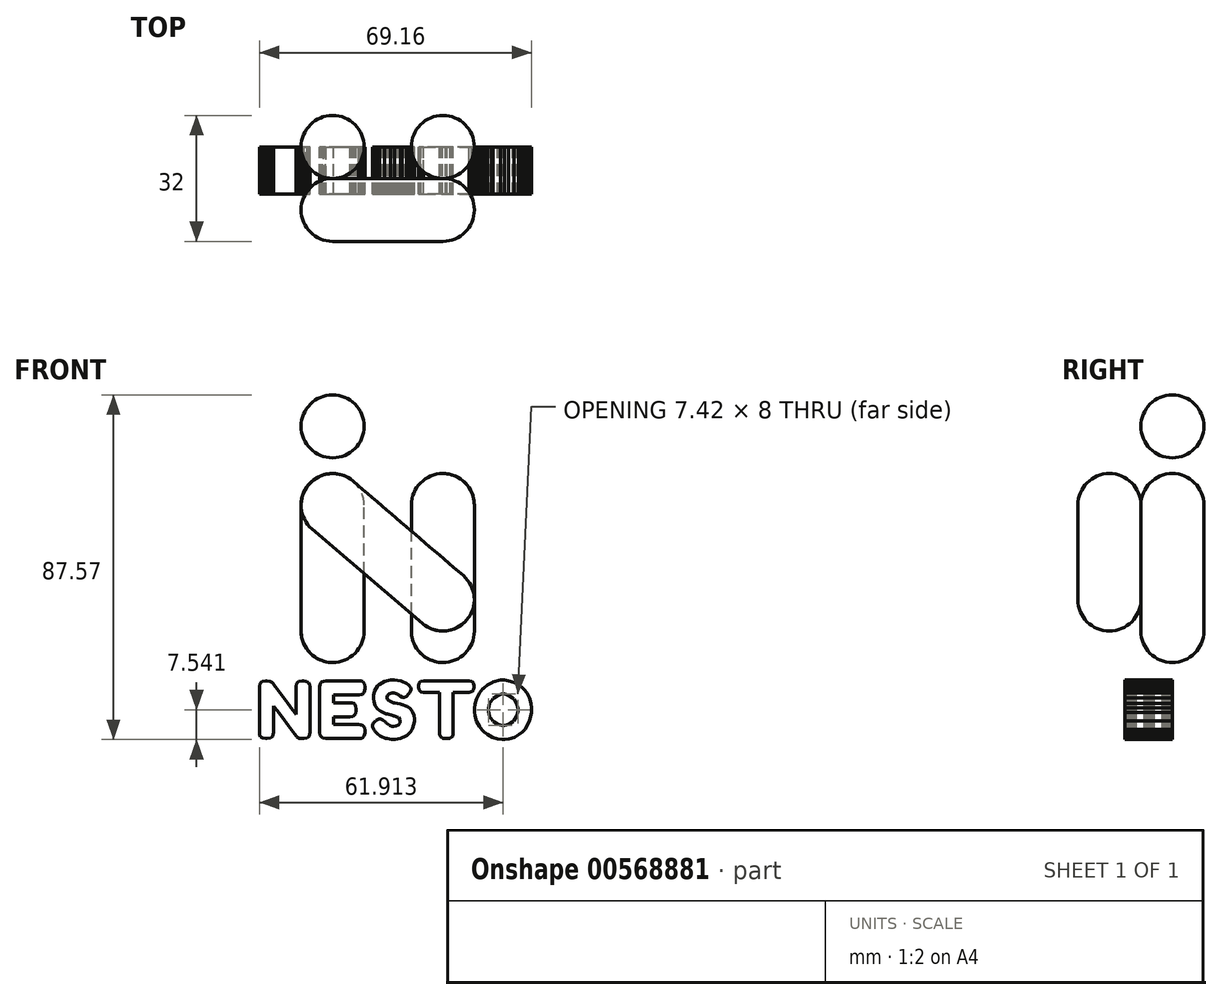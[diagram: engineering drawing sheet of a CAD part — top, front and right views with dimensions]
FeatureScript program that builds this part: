
annotation { "Feature Type Name" : "Feature", "Feature Type Description" : "" }
export const myFeature = defineFeature(function(context is Context, id is Id, definition is map)
    precondition{}
    {
        {
            var Q0;
            Q0=qCreatedBy(makeId("Front.planeOp"),FACE);
            var sketch = newSketch(context, id + "F0", { "sketchPlane" : qUnion([Q0])});
            skLineSegment(sketch, "E0.bottom", {"start": v(0, 0) * mm, "end": v(16, 0) * mm, "construction": true});
            skLineSegment(sketch, "E0.top", {"start": v(0, 32) * mm, "end": v(16, 32) * mm, "construction": true});
            skLineSegment(sketch, "E0.left", {"start": v(0, 0) * mm, "end": v(0, 32) * mm});
            skLineSegment(sketch, "E0.right", {"start": v(16, 0) * mm, "end": v(16, 32) * mm});
            skArc(sketch, "E1", {"start": v(0, 32) * mm, "mid": v(8, 40) * mm, "end": v(16, 32) * mm});
            skArc(sketch, "E2", {"start": v(0, 0) * mm, "mid": v(8, -8) * mm, "end": v(16, 0) * mm});
            skArc(sketch, "E3.1.0.0", {"start": v(28, 0) * mm, "mid": v(36, -8) * mm, "end": v(44, 0) * mm});
            skArc(sketch, "E3.1.0.1", {"start": v(28, 32) * mm, "mid": v(36, 40) * mm, "end": v(44, 32) * mm});
            skLineSegment(sketch, "E3.1.0.2", {"start": v(44, 0) * mm, "end": v(44, 32) * mm});
            skLineSegment(sketch, "E3.1.0.3", {"start": v(28, 0) * mm, "end": v(28, 32) * mm});
            skLineSegment(sketch, "E3.1.0.4", {"start": v(28, 32) * mm, "end": v(44, 32) * mm, "construction": true});
            skLineSegment(sketch, "E3.1.0.5", {"start": v(28, 0) * mm, "end": v(44, 0) * mm, "construction": true});
            skLineSegment(sketch, "E3.direction1", {"start": v(0, 0) * mm, "end": v(28, 0) * mm, "construction": true});
            skLineSegment(sketch, "E4", {"start": v(8, 40) * mm, "end": v(8, -8) * mm});
            skLineSegment(sketch, "E5", {"start": v(36, 40) * mm, "end": v(36, -8) * mm});
            skLineSegment(sketch, "E6", {"start": v(8, 32) * mm, "end": v(36, 8) * mm, "construction": true});
            skCircle(sketch, "E7", {"center": v(36, 8) * mm, "radius": 8 * mm, "construction": true});
            skCircle(sketch, "E8", {"center": v(8, 52) * mm, "radius": 8 * mm});
            skLineSegment(sketch, "E9", {"start": v(8, 60) * mm, "end": v(8, 44) * mm});
            skSolve(sketch);
        }
        {
            var Q0;
            {var subQ0=sQuery(id+"F0.wireOp",EDGE,"E0.left");Q0=makeQuery(id+"F0.imprint","IMPRINT",FACE,{"disambiguationData":[TD([[makeQuery(id+"F0.imprint","IMPRINT",EDGE,{"derivedFrom":subQ0}),-1.0]])]});}
            var Q1;
            Q1=sQuery(id+"F0.wireOp",EDGE,"E4");
            revolve(context, id + "F1", {"entities" : qUnion([Q0]), "axis" : qUnion([Q1]), "revolveType" : RevolveType.FULL});
        }
        {
            var Q0;
            {var subQ0=sQuery(id+"F0.wireOp",EDGE,"E3.1.0.3");Q0=makeQuery(id+"F0.imprint","IMPRINT",FACE,{"disambiguationData":[TD([[makeQuery(id+"F0.imprint","IMPRINT",EDGE,{"derivedFrom":subQ0}),-1.0]])]});}
            var Q1;
            Q1=sQuery(id+"F0.wireOp",EDGE,"E5");
            revolve(context, id + "F2", {"entities" : qUnion([Q0]), "axis" : qUnion([Q1]), "revolveType" : RevolveType.FULL});
        }
        {
            var Q0;
            {var subQ0=sQuery(id+"F0.wireOp",EDGE,"E9");Q0=makeQuery(id+"F0.imprint","IMPRINT",FACE,{"disambiguationData":[TD([[makeQuery(id+"F0.imprint","IMPRINT",EDGE,{"derivedFrom":subQ0}),-1.0]])]});}
            var Q1;
            Q1=sQuery(id+"F0.wireOp",EDGE,"E9");
            revolve(context, id + "F3", {"entities" : qUnion([Q0]), "axis" : qUnion([Q1]), "revolveType" : RevolveType.FULL});
        }
        {
            var Q0;
            Q0=qCreatedBy(makeId("Front.planeOp"),FACE);
            var sketch = newSketch(context, id + "F4", { "sketchPlane" : qUnion([Q0])});
            skLineSegment(sketch, "E10.0", {"start": v(1.93, 37.2) * mm, "end": v(42.07, 2.8) * mm});
            skArc(sketch, "E11.0", {"start": v(42.07, 2.8) * mm, "mid": v(43.98, 8.61) * mm, "end": v(41.2, 14.07) * mm});
            skArc(sketch, "E12", {"start": v(13.2, 38.07) * mm, "mid": v(7.39, 39.98) * mm, "end": v(1.93, 37.2) * mm});
            skLineSegment(sketch, "E13", {"start": v(8, 32) * mm, "end": v(13.2, 38.07) * mm, "construction": true});
            skLineSegment(sketch, "E14", {"start": v(13.2, 38.07) * mm, "end": v(41.2, 14.07) * mm});
            skSolve(sketch);
        }
        {
            var Q0;
            Q0=makeQuery(id+"F4.imprint","IMPRINT",FACE,{"disambiguationData":[TD([[makeQuery(id+"F4.imprint","IMPRINT",EDGE,{"derivedFrom":sQuery(id+"F4.wireOp",EDGE,"E10.0")}),1.0]])]});
            var Q1;
            Q1=sQuery(id+"F4.wireOp",EDGE,"E10.0");
            revolve(context, id + "F5", {"entities" : qUnion([Q0]), "axis" : qUnion([Q1]), "revolveType" : RevolveType.FULL});
        }
        {
            var Q0;
            Q0=makeQuery(id+"F5.opRevolve","SWEPT_BODY",BODY,{"disambiguationData":[OSD([sQuery(id+"F4.wireOp",EDGE,"E10.0"),sQuery(id+"F4.wireOp",EDGE,"E11.0"),sQuery(id+"F4.wireOp",EDGE,"E12"),sQuery(id+"F4.wireOp",EDGE,"E14")])]});
            transform(context, id + "F6", {"entities" : qUnion([Q0]), "transformType" : TransformType.TRANSLATION_3D, "dx" : 0 * mm, "dy" : -16 * mm, "dz" : 0 * mm, "makeCopy" : false});
        }
        {
            var Q0;
            Q0=qCreatedBy(makeId("Front.planeOp"),FACE);
            var sketch = newSketch(context, id + "F7", { "sketchPlane" : qUnion([Q0])});
            skLineSegment(sketch, "E15", {"start": v(-1.05, 0.28) * mm, "end": v(-1.05, 0.28) * mm});
            skLineSegment(sketch, "E16", {"start": v(-1.05, 0.28) * mm, "end": v(-1.03, 0.3) * mm});
            skLineSegment(sketch, "E17", {"start": v(-1.03, 0.3) * mm, "end": v(-1.02, 0.3) * mm});
            skLineSegment(sketch, "E18", {"start": v(-1.02, 0.3) * mm, "end": v(-1.02, 0.3) * mm});
            skLineSegment(sketch, "E19", {"start": v(-1.02, 0.3) * mm, "end": v(-1, 0.3) * mm});
            skLineSegment(sketch, "E20", {"start": v(-1, 0.3) * mm, "end": v(-0.98, 0.3) * mm});
            skLineSegment(sketch, "E21", {"start": v(-0.98, 0.3) * mm, "end": v(-0.97, 0.3) * mm});
            skLineSegment(sketch, "E22", {"start": v(-0.97, 0.3) * mm, "end": v(-0.95, 0.3) * mm});
            skLineSegment(sketch, "E23", {"start": v(-0.95, 0.3) * mm, "end": v(-0.94, 0.3) * mm});
            skLineSegment(sketch, "E24", {"start": v(-0.94, 0.3) * mm, "end": v(-0.94, 0.3) * mm});
            skLineSegment(sketch, "E25", {"start": v(-0.94, 0.3) * mm, "end": v(-0.92, 0.3) * mm});
            skLineSegment(sketch, "E26", {"start": v(-0.92, 0.3) * mm, "end": v(-0.92, 0.3) * mm});
            skLineSegment(sketch, "E27", {"start": v(-0.92, 0.3) * mm, "end": v(-0.92, 0.29) * mm});
            skLineSegment(sketch, "E28", {"start": v(-0.92, 0.29) * mm, "end": v(-0.91, 0.27) * mm});
            skLineSegment(sketch, "E29", {"start": v(-0.91, 0.27) * mm, "end": v(-0.91, 0.27) * mm});
            skLineSegment(sketch, "E30", {"start": v(-0.91, 0.27) * mm, "end": v(-0.9, 0.24) * mm});
            skLineSegment(sketch, "E31", {"start": v(-0.9, 0.24) * mm, "end": v(-0.9, 0.23) * mm});
            skLineSegment(sketch, "E32", {"start": v(-0.9, 0.23) * mm, "end": v(-0.9, -0.23) * mm});
            skLineSegment(sketch, "E33", {"start": v(-0.9, -0.23) * mm, "end": v(-0.9, -0.24) * mm});
            skLineSegment(sketch, "E34", {"start": v(-0.9, -0.24) * mm, "end": v(-0.9, -0.26) * mm});
            skLineSegment(sketch, "E35", {"start": v(-0.9, -0.26) * mm, "end": v(-0.9, -0.26) * mm});
            skLineSegment(sketch, "E36", {"start": v(-0.9, -0.26) * mm, "end": v(-0.92, -0.28) * mm});
            skLineSegment(sketch, "E37", {"start": v(-0.92, -0.28) * mm, "end": v(-0.92, -0.28) * mm});
            skLineSegment(sketch, "E38", {"start": v(-0.92, -0.28) * mm, "end": v(-0.92, -0.29) * mm});
            skLineSegment(sketch, "E39", {"start": v(-0.92, -0.29) * mm, "end": v(-0.94, -0.3) * mm});
            skLineSegment(sketch, "E40", {"start": v(-0.94, -0.3) * mm, "end": v(-0.97, -0.3) * mm});
            skLineSegment(sketch, "E41", {"start": v(-0.97, -0.3) * mm, "end": v(-0.98, -0.3) * mm});
            skLineSegment(sketch, "E42", {"start": v(-0.98, -0.3) * mm, "end": v(-1, -0.3) * mm});
            skLineSegment(sketch, "E43", {"start": v(-1, -0.3) * mm, "end": v(-1.02, -0.3) * mm});
            skLineSegment(sketch, "E44", {"start": v(-1.02, -0.3) * mm, "end": v(-1.03, -0.3) * mm});
            skLineSegment(sketch, "E45", {"start": v(-1.03, -0.3) * mm, "end": v(-1.03, -0.3) * mm});
            skLineSegment(sketch, "E46", {"start": v(-1.03, -0.3) * mm, "end": v(-1.05, -0.29) * mm});
            skLineSegment(sketch, "E47", {"start": v(-1.05, -0.29) * mm, "end": v(-1.05, -0.28) * mm});
            skLineSegment(sketch, "E48", {"start": v(-1.05, -0.28) * mm, "end": v(-1.07, -0.26) * mm});
            skLineSegment(sketch, "E49", {"start": v(-1.07, -0.26) * mm, "end": v(-1.13, -0.17) * mm});
            skLineSegment(sketch, "E50", {"start": v(-1.13, -0.17) * mm, "end": v(-1.2, -0.08) * mm});
            skLineSegment(sketch, "E51", {"start": v(-1.2, -0.08) * mm, "end": v(-1.26, 0) * mm});
            skLineSegment(sketch, "E52", {"start": v(-1.26, 0) * mm, "end": v(-1.28, 0.03) * mm});
            skLineSegment(sketch, "E53", {"start": v(-1.28, 0.03) * mm, "end": v(-1.3, 0.04) * mm});
            skLineSegment(sketch, "E54", {"start": v(-1.3, 0.04) * mm, "end": v(-1.3, -0.23) * mm});
            skLineSegment(sketch, "E55", {"start": v(-1.3, -0.23) * mm, "end": v(-1.3, -0.24) * mm});
            skLineSegment(sketch, "E56", {"start": v(-1.3, -0.24) * mm, "end": v(-1.3, -0.26) * mm});
            skLineSegment(sketch, "E57", {"start": v(-1.3, -0.26) * mm, "end": v(-1.3, -0.26) * mm});
            skLineSegment(sketch, "E58", {"start": v(-1.3, -0.26) * mm, "end": v(-1.3, -0.28) * mm});
            skLineSegment(sketch, "E59", {"start": v(-1.3, -0.28) * mm, "end": v(-1.3, -0.28) * mm});
            skLineSegment(sketch, "E60", {"start": v(-1.3, -0.28) * mm, "end": v(-1.3, -0.29) * mm});
            skLineSegment(sketch, "E61", {"start": v(-1.3, -0.29) * mm, "end": v(-1.33, -0.3) * mm});
            skLineSegment(sketch, "E62", {"start": v(-1.33, -0.3) * mm, "end": v(-1.36, -0.3) * mm});
            skLineSegment(sketch, "E63", {"start": v(-1.36, -0.3) * mm, "end": v(-1.37, -0.3) * mm});
            skLineSegment(sketch, "E64", {"start": v(-1.37, -0.3) * mm, "end": v(-1.38, -0.3) * mm});
            skLineSegment(sketch, "E65", {"start": v(-1.38, -0.3) * mm, "end": v(-1.41, -0.3) * mm});
            skLineSegment(sketch, "E66", {"start": v(-1.41, -0.3) * mm, "end": v(-1.43, -0.29) * mm});
            skLineSegment(sketch, "E67", {"start": v(-1.43, -0.29) * mm, "end": v(-1.43, -0.28) * mm});
            skLineSegment(sketch, "E68", {"start": v(-1.43, -0.28) * mm, "end": v(-1.43, -0.28) * mm});
            skLineSegment(sketch, "E69", {"start": v(-1.43, -0.28) * mm, "end": v(-1.44, -0.26) * mm});
            skLineSegment(sketch, "E70", {"start": v(-1.44, -0.26) * mm, "end": v(-1.44, -0.26) * mm});
            skLineSegment(sketch, "E71", {"start": v(-1.44, -0.26) * mm, "end": v(-1.44, -0.24) * mm});
            skLineSegment(sketch, "E72", {"start": v(-1.44, -0.24) * mm, "end": v(-1.44, -0.23) * mm});
            skLineSegment(sketch, "E73", {"start": v(-1.44, -0.23) * mm, "end": v(-1.44, 0.23) * mm});
            skLineSegment(sketch, "E74", {"start": v(-1.44, 0.23) * mm, "end": v(-1.44, 0.25) * mm});
            skLineSegment(sketch, "E75", {"start": v(-1.44, 0.25) * mm, "end": v(-1.43, 0.28) * mm});
            skLineSegment(sketch, "E76", {"start": v(-1.43, 0.28) * mm, "end": v(-1.43, 0.28) * mm});
            skLineSegment(sketch, "E77", {"start": v(-1.43, 0.28) * mm, "end": v(-1.41, 0.3) * mm});
            skLineSegment(sketch, "E78", {"start": v(-1.41, 0.3) * mm, "end": v(-1.4, 0.3) * mm});
            skLineSegment(sketch, "E79", {"start": v(-1.4, 0.3) * mm, "end": v(-1.4, 0.3) * mm});
            skLineSegment(sketch, "E80", {"start": v(-1.4, 0.3) * mm, "end": v(-1.38, 0.3) * mm});
            skLineSegment(sketch, "E81", {"start": v(-1.38, 0.3) * mm, "end": v(-1.37, 0.3) * mm});
            skLineSegment(sketch, "E82", {"start": v(-1.37, 0.3) * mm, "end": v(-1.36, 0.3) * mm});
            skLineSegment(sketch, "E83", {"start": v(-1.36, 0.3) * mm, "end": v(-1.33, 0.3) * mm});
            skLineSegment(sketch, "E84", {"start": v(-1.33, 0.3) * mm, "end": v(-1.33, 0.3) * mm});
            skLineSegment(sketch, "E85", {"start": v(-1.33, 0.3) * mm, "end": v(-1.3, 0.3) * mm});
            skLineSegment(sketch, "E86", {"start": v(-1.3, 0.3) * mm, "end": v(-1.3, 0.29) * mm});
            skLineSegment(sketch, "E87", {"start": v(-1.3, 0.29) * mm, "end": v(-1.3, 0.29) * mm});
            skLineSegment(sketch, "E88", {"start": v(-1.3, 0.29) * mm, "end": v(-1.3, 0.28) * mm});
            skLineSegment(sketch, "E89", {"start": v(-1.3, 0.28) * mm, "end": v(-1.3, 0.27) * mm});
            skLineSegment(sketch, "E90", {"start": v(-1.3, 0.27) * mm, "end": v(-1.29, 0.27) * mm});
            skLineSegment(sketch, "E91", {"start": v(-1.29, 0.27) * mm, "end": v(-1.27, 0.24) * mm});
            skLineSegment(sketch, "E92", {"start": v(-1.27, 0.24) * mm, "end": v(-1.2, 0.16) * mm});
            skLineSegment(sketch, "E93", {"start": v(-1.2, 0.16) * mm, "end": v(-1.14, 0.07) * mm});
            skLineSegment(sketch, "E94", {"start": v(-1.14, 0.07) * mm, "end": v(-1.1, 0) * mm});
            skLineSegment(sketch, "E95", {"start": v(-1.1, 0) * mm, "end": v(-1.06, -0.04) * mm});
            skLineSegment(sketch, "E96", {"start": v(-1.06, -0.04) * mm, "end": v(-1.05, -0.05) * mm});
            skLineSegment(sketch, "E97", {"start": v(-1.05, -0.05) * mm, "end": v(-1.05, 0.23) * mm});
            skLineSegment(sketch, "E98", {"start": v(-1.05, 0.23) * mm, "end": v(-1.05, 0.25) * mm});
            skLineSegment(sketch, "E99", {"start": v(-1.05, 0.25) * mm, "end": v(-1.05, 0.28) * mm});
            skLineSegment(sketch, "E100", {"start": v(-0.66, -0.16) * mm, "end": v(-0.4, -0.16) * mm});
            skLineSegment(sketch, "E101", {"start": v(-0.4, -0.16) * mm, "end": v(-0.4, -0.16) * mm});
            skLineSegment(sketch, "E102", {"start": v(-0.4, -0.16) * mm, "end": v(-0.37, -0.16) * mm});
            skLineSegment(sketch, "E103", {"start": v(-0.37, -0.16) * mm, "end": v(-0.37, -0.16) * mm});
            skLineSegment(sketch, "E104", {"start": v(-0.37, -0.16) * mm, "end": v(-0.35, -0.17) * mm});
            skLineSegment(sketch, "E105", {"start": v(-0.35, -0.17) * mm, "end": v(-0.35, -0.17) * mm});
            skLineSegment(sketch, "E106", {"start": v(-0.35, -0.17) * mm, "end": v(-0.34, -0.17) * mm});
            skLineSegment(sketch, "E107", {"start": v(-0.34, -0.17) * mm, "end": v(-0.33, -0.19) * mm});
            skLineSegment(sketch, "E108", {"start": v(-0.33, -0.19) * mm, "end": v(-0.33, -0.22) * mm});
            skLineSegment(sketch, "E109", {"start": v(-0.33, -0.22) * mm, "end": v(-0.33, -0.23) * mm});
            skLineSegment(sketch, "E110", {"start": v(-0.33, -0.23) * mm, "end": v(-0.33, -0.24) * mm});
            skLineSegment(sketch, "E111", {"start": v(-0.33, -0.24) * mm, "end": v(-0.33, -0.28) * mm});
            skLineSegment(sketch, "E112", {"start": v(-0.33, -0.28) * mm, "end": v(-0.35, -0.3) * mm});
            skLineSegment(sketch, "E113", {"start": v(-0.35, -0.3) * mm, "end": v(-0.36, -0.3) * mm});
            skLineSegment(sketch, "E114", {"start": v(-0.36, -0.3) * mm, "end": v(-0.36, -0.3) * mm});
            skLineSegment(sketch, "E115", {"start": v(-0.36, -0.3) * mm, "end": v(-0.39, -0.3) * mm});
            skLineSegment(sketch, "E116", {"start": v(-0.39, -0.3) * mm, "end": v(-0.4, -0.3) * mm});
            skLineSegment(sketch, "E117", {"start": v(-0.4, -0.3) * mm, "end": v(-0.73, -0.3) * mm});
            skLineSegment(sketch, "E118", {"start": v(-0.73, -0.3) * mm, "end": v(-0.74, -0.3) * mm});
            skLineSegment(sketch, "E119", {"start": v(-0.74, -0.3) * mm, "end": v(-0.78, -0.3) * mm});
            skLineSegment(sketch, "E120", {"start": v(-0.78, -0.3) * mm, "end": v(-0.8, -0.28) * mm});
            skLineSegment(sketch, "E121", {"start": v(-0.8, -0.28) * mm, "end": v(-0.8, -0.27) * mm});
            skLineSegment(sketch, "E122", {"start": v(-0.8, -0.27) * mm, "end": v(-0.8, -0.27) * mm});
            skLineSegment(sketch, "E123", {"start": v(-0.8, -0.27) * mm, "end": v(-0.8, -0.24) * mm});
            skLineSegment(sketch, "E124", {"start": v(-0.8, -0.24) * mm, "end": v(-0.8, -0.23) * mm});
            skLineSegment(sketch, "E125", {"start": v(-0.8, -0.23) * mm, "end": v(-0.8, 0.23) * mm});
            skLineSegment(sketch, "E126", {"start": v(-0.8, 0.23) * mm, "end": v(-0.8, 0.24) * mm});
            skLineSegment(sketch, "E127", {"start": v(-0.8, 0.24) * mm, "end": v(-0.8, 0.27) * mm});
            skLineSegment(sketch, "E128", {"start": v(-0.8, 0.27) * mm, "end": v(-0.79, 0.29) * mm});
            skLineSegment(sketch, "E129", {"start": v(-0.79, 0.29) * mm, "end": v(-0.79, 0.3) * mm});
            skLineSegment(sketch, "E130", {"start": v(-0.79, 0.3) * mm, "end": v(-0.78, 0.3) * mm});
            skLineSegment(sketch, "E131", {"start": v(-0.78, 0.3) * mm, "end": v(-0.76, 0.3) * mm});
            skLineSegment(sketch, "E132", {"start": v(-0.76, 0.3) * mm, "end": v(-0.74, 0.3) * mm});
            skLineSegment(sketch, "E133", {"start": v(-0.74, 0.3) * mm, "end": v(-0.73, 0.3) * mm});
            skLineSegment(sketch, "E134", {"start": v(-0.73, 0.3) * mm, "end": v(-0.4, 0.3) * mm});
            skLineSegment(sketch, "E135", {"start": v(-0.4, 0.3) * mm, "end": v(-0.4, 0.3) * mm});
            skLineSegment(sketch, "E136", {"start": v(-0.4, 0.3) * mm, "end": v(-0.37, 0.3) * mm});
            skLineSegment(sketch, "E137", {"start": v(-0.37, 0.3) * mm, "end": v(-0.37, 0.3) * mm});
            skLineSegment(sketch, "E138", {"start": v(-0.37, 0.3) * mm, "end": v(-0.35, 0.3) * mm});
            skLineSegment(sketch, "E139", {"start": v(-0.35, 0.3) * mm, "end": v(-0.35, 0.3) * mm});
            skLineSegment(sketch, "E140", {"start": v(-0.35, 0.3) * mm, "end": v(-0.34, 0.3) * mm});
            skLineSegment(sketch, "E141", {"start": v(-0.34, 0.3) * mm, "end": v(-0.33, 0.27) * mm});
            skLineSegment(sketch, "E142", {"start": v(-0.33, 0.27) * mm, "end": v(-0.33, 0.24) * mm});
            skLineSegment(sketch, "E143", {"start": v(-0.33, 0.24) * mm, "end": v(-0.33, 0.23) * mm});
            skLineSegment(sketch, "E144", {"start": v(-0.33, 0.23) * mm, "end": v(-0.33, 0.22) * mm});
            skLineSegment(sketch, "E145", {"start": v(-0.33, 0.22) * mm, "end": v(-0.33, 0.19) * mm});
            skLineSegment(sketch, "E146", {"start": v(-0.33, 0.19) * mm, "end": v(-0.35, 0.16) * mm});
            skLineSegment(sketch, "E147", {"start": v(-0.35, 0.16) * mm, "end": v(-0.36, 0.16) * mm});
            skLineSegment(sketch, "E148", {"start": v(-0.36, 0.16) * mm, "end": v(-0.36, 0.16) * mm});
            skLineSegment(sketch, "E149", {"start": v(-0.36, 0.16) * mm, "end": v(-0.39, 0.16) * mm});
            skLineSegment(sketch, "E150", {"start": v(-0.39, 0.16) * mm, "end": v(-0.4, 0.16) * mm});
            skLineSegment(sketch, "E151", {"start": v(-0.4, 0.16) * mm, "end": v(-0.66, 0.16) * mm});
            skLineSegment(sketch, "E152", {"start": v(-0.66, 0.16) * mm, "end": v(-0.66, 0.07) * mm});
            skLineSegment(sketch, "E153", {"start": v(-0.66, 0.07) * mm, "end": v(-0.5, 0.07) * mm});
            skLineSegment(sketch, "E154", {"start": v(-0.5, 0.07) * mm, "end": v(-0.48, 0.07) * mm});
            skLineSegment(sketch, "E155", {"start": v(-0.48, 0.07) * mm, "end": v(-0.46, 0.07) * mm});
            skLineSegment(sketch, "E156", {"start": v(-0.46, 0.07) * mm, "end": v(-0.46, 0.07) * mm});
            skLineSegment(sketch, "E157", {"start": v(-0.46, 0.07) * mm, "end": v(-0.44, 0.07) * mm});
            skLineSegment(sketch, "E158", {"start": v(-0.44, 0.07) * mm, "end": v(-0.44, 0.06) * mm});
            skLineSegment(sketch, "E159", {"start": v(-0.44, 0.06) * mm, "end": v(-0.44, 0.06) * mm});
            skLineSegment(sketch, "E160", {"start": v(-0.44, 0.06) * mm, "end": v(-0.42, 0.04) * mm});
            skLineSegment(sketch, "E161", {"start": v(-0.42, 0.04) * mm, "end": v(-0.42, 0.01) * mm});
            skLineSegment(sketch, "E162", {"start": v(-0.42, 0.01) * mm, "end": v(-0.42, 0) * mm});
            skLineSegment(sketch, "E163", {"start": v(-0.42, 0) * mm, "end": v(-0.42, -0.01) * mm});
            skLineSegment(sketch, "E164", {"start": v(-0.42, -0.01) * mm, "end": v(-0.42, -0.05) * mm});
            skLineSegment(sketch, "E165", {"start": v(-0.42, -0.05) * mm, "end": v(-0.44, -0.07) * mm});
            skLineSegment(sketch, "E166", {"start": v(-0.44, -0.07) * mm, "end": v(-0.45, -0.07) * mm});
            skLineSegment(sketch, "E167", {"start": v(-0.45, -0.07) * mm, "end": v(-0.45, -0.07) * mm});
            skLineSegment(sketch, "E168", {"start": v(-0.45, -0.07) * mm, "end": v(-0.48, -0.07) * mm});
            skLineSegment(sketch, "E169", {"start": v(-0.48, -0.07) * mm, "end": v(-0.5, -0.07) * mm});
            skLineSegment(sketch, "E170", {"start": v(-0.5, -0.07) * mm, "end": v(-0.66, -0.07) * mm});
            skLineSegment(sketch, "E171", {"start": v(-0.66, -0.07) * mm, "end": v(-0.66, -0.16) * mm});
            skLineSegment(sketch, "E172", {"start": v(-0.22, -0.22) * mm, "end": v(-0.23, -0.22) * mm});
            skLineSegment(sketch, "E173", {"start": v(-0.23, -0.22) * mm, "end": v(-0.25, -0.18) * mm});
            skLineSegment(sketch, "E174", {"start": v(-0.25, -0.18) * mm, "end": v(-0.25, -0.17) * mm});
            skLineSegment(sketch, "E175", {"start": v(-0.25, -0.17) * mm, "end": v(-0.25, -0.17) * mm});
            skLineSegment(sketch, "E176", {"start": v(-0.25, -0.17) * mm, "end": v(-0.24, -0.15) * mm});
            skLineSegment(sketch, "E177", {"start": v(-0.24, -0.15) * mm, "end": v(-0.22, -0.12) * mm});
            skLineSegment(sketch, "E178", {"start": v(-0.22, -0.12) * mm, "end": v(-0.21, -0.12) * mm});
            skLineSegment(sketch, "E179", {"start": v(-0.21, -0.12) * mm, "end": v(-0.2, -0.11) * mm});
            skLineSegment(sketch, "E180", {"start": v(-0.2, -0.11) * mm, "end": v(-0.18, -0.1) * mm});
            skLineSegment(sketch, "E181", {"start": v(-0.18, -0.1) * mm, "end": v(-0.17, -0.1) * mm});
            skLineSegment(sketch, "E182", {"start": v(-0.17, -0.1) * mm, "end": v(-0.16, -0.1) * mm});
            skLineSegment(sketch, "E183", {"start": v(-0.16, -0.1) * mm, "end": v(-0.14, -0.1) * mm});
            skLineSegment(sketch, "E184", {"start": v(-0.14, -0.1) * mm, "end": v(-0.1, -0.13) * mm});
            skLineSegment(sketch, "E185", {"start": v(-0.1, -0.13) * mm, "end": v(-0.1, -0.14) * mm});
            skLineSegment(sketch, "E186", {"start": v(-0.1, -0.14) * mm, "end": v(-0.1, -0.14) * mm});
            skLineSegment(sketch, "E187", {"start": v(-0.1, -0.14) * mm, "end": v(-0.07, -0.16) * mm});
            skLineSegment(sketch, "E188", {"start": v(-0.07, -0.16) * mm, "end": v(-0.07, -0.16) * mm});
            skLineSegment(sketch, "E189", {"start": v(-0.07, -0.16) * mm, "end": v(-0.06, -0.17) * mm});
            skLineSegment(sketch, "E190", {"start": v(-0.06, -0.17) * mm, "end": v(-0.04, -0.18) * mm});
            skLineSegment(sketch, "E191", {"start": v(-0.04, -0.18) * mm, "end": v(-0.03, -0.18) * mm});
            skLineSegment(sketch, "E192", {"start": v(-0.03, -0.18) * mm, "end": v(-0.02, -0.18) * mm});
            skLineSegment(sketch, "E193", {"start": v(-0.02, -0.18) * mm, "end": v(0, -0.17) * mm});
            skLineSegment(sketch, "E194", {"start": v(0, -0.17) * mm, "end": v(0.03, -0.16) * mm});
            skLineSegment(sketch, "E195", {"start": v(0.03, -0.16) * mm, "end": v(0.04, -0.14) * mm});
            skLineSegment(sketch, "E196", {"start": v(0.04, -0.14) * mm, "end": v(0.05, -0.12) * mm});
            skLineSegment(sketch, "E197", {"start": v(0.05, -0.12) * mm, "end": v(0.05, -0.11) * mm});
            skLineSegment(sketch, "E198", {"start": v(0.05, -0.11) * mm, "end": v(0.05, -0.1) * mm});
            skLineSegment(sketch, "E199", {"start": v(0.05, -0.1) * mm, "end": v(0.03, -0.08) * mm});
            skLineSegment(sketch, "E200", {"start": v(0.03, -0.08) * mm, "end": v(0.03, -0.08) * mm});
            skLineSegment(sketch, "E201", {"start": v(0.03, -0.08) * mm, "end": v(-0.02, -0.06) * mm});
            skLineSegment(sketch, "E202", {"start": v(-0.02, -0.06) * mm, "end": v(-0.02, -0.06) * mm});
            skLineSegment(sketch, "E203", {"start": v(-0.02, -0.06) * mm, "end": v(-0.03, -0.06) * mm});
            skLineSegment(sketch, "E204", {"start": v(-0.03, -0.06) * mm, "end": v(-0.09, -0.05) * mm});
            skLineSegment(sketch, "E205", {"start": v(-0.09, -0.05) * mm, "end": v(-0.1, -0.04) * mm});
            skLineSegment(sketch, "E206", {"start": v(-0.1, -0.04) * mm, "end": v(-0.1, -0.04) * mm});
            skLineSegment(sketch, "E207", {"start": v(-0.1, -0.04) * mm, "end": v(-0.16, -0.02) * mm});
            skLineSegment(sketch, "E208", {"start": v(-0.16, -0.02) * mm, "end": v(-0.16, -0.01) * mm});
            skLineSegment(sketch, "E209", {"start": v(-0.16, -0.01) * mm, "end": v(-0.17, -0.01) * mm});
            skLineSegment(sketch, "E210", {"start": v(-0.17, -0.01) * mm, "end": v(-0.2, 0) * mm});
            skLineSegment(sketch, "E211", {"start": v(-0.2, 0) * mm, "end": v(-0.21, 0.04) * mm});
            skLineSegment(sketch, "E212", {"start": v(-0.21, 0.04) * mm, "end": v(-0.21, 0.04) * mm});
            skLineSegment(sketch, "E213", {"start": v(-0.21, 0.04) * mm, "end": v(-0.22, 0.05) * mm});
            skLineSegment(sketch, "E214", {"start": v(-0.22, 0.05) * mm, "end": v(-0.23, 0.08) * mm});
            skLineSegment(sketch, "E215", {"start": v(-0.23, 0.08) * mm, "end": v(-0.24, 0.12) * mm});
            skLineSegment(sketch, "E216", {"start": v(-0.24, 0.12) * mm, "end": v(-0.24, 0.13) * mm});
            skLineSegment(sketch, "E217", {"start": v(-0.24, 0.13) * mm, "end": v(-0.24, 0.15) * mm});
            skLineSegment(sketch, "E218", {"start": v(-0.24, 0.15) * mm, "end": v(-0.22, 0.2) * mm});
            skLineSegment(sketch, "E219", {"start": v(-0.22, 0.2) * mm, "end": v(-0.19, 0.25) * mm});
            skLineSegment(sketch, "E220", {"start": v(-0.19, 0.25) * mm, "end": v(-0.18, 0.26) * mm});
            skLineSegment(sketch, "E221", {"start": v(-0.18, 0.26) * mm, "end": v(-0.17, 0.27) * mm});
            skLineSegment(sketch, "E222", {"start": v(-0.17, 0.27) * mm, "end": v(-0.12, 0.3) * mm});
            skLineSegment(sketch, "E223", {"start": v(-0.12, 0.3) * mm, "end": v(-0.05, 0.32) * mm});
            skLineSegment(sketch, "E224", {"start": v(-0.05, 0.32) * mm, "end": v(-0.03, 0.32) * mm});
            skLineSegment(sketch, "E225", {"start": v(-0.03, 0.32) * mm, "end": v(0, 0.32) * mm});
            skLineSegment(sketch, "E226", {"start": v(0, 0.32) * mm, "end": v(0.05, 0.3) * mm});
            skLineSegment(sketch, "E227", {"start": v(0.05, 0.3) * mm, "end": v(0.06, 0.3) * mm});
            skLineSegment(sketch, "E228", {"start": v(0.06, 0.3) * mm, "end": v(0.07, 0.3) * mm});
            skLineSegment(sketch, "E229", {"start": v(0.07, 0.3) * mm, "end": v(0.11, 0.28) * mm});
            skLineSegment(sketch, "E230", {"start": v(0.11, 0.28) * mm, "end": v(0.12, 0.28) * mm});
            skLineSegment(sketch, "E231", {"start": v(0.12, 0.28) * mm, "end": v(0.14, 0.26) * mm});
            skLineSegment(sketch, "E232", {"start": v(0.14, 0.26) * mm, "end": v(0.14, 0.26) * mm});
            skLineSegment(sketch, "E233", {"start": v(0.14, 0.26) * mm, "end": v(0.16, 0.24) * mm});
            skLineSegment(sketch, "E234", {"start": v(0.16, 0.24) * mm, "end": v(0.16, 0.22) * mm});
            skLineSegment(sketch, "E235", {"start": v(0.16, 0.22) * mm, "end": v(0.16, 0.22) * mm});
            skLineSegment(sketch, "E236", {"start": v(0.16, 0.22) * mm, "end": v(0.16, 0.21) * mm});
            skLineSegment(sketch, "E237", {"start": v(0.16, 0.21) * mm, "end": v(0.16, 0.2) * mm});
            skLineSegment(sketch, "E238", {"start": v(0.16, 0.2) * mm, "end": v(0.15, 0.18) * mm});
            skLineSegment(sketch, "E239", {"start": v(0.15, 0.18) * mm, "end": v(0.14, 0.17) * mm});
            skLineSegment(sketch, "E240", {"start": v(0.14, 0.17) * mm, "end": v(0.14, 0.17) * mm});
            skLineSegment(sketch, "E241", {"start": v(0.14, 0.17) * mm, "end": v(0.11, 0.14) * mm});
            skLineSegment(sketch, "E242", {"start": v(0.11, 0.14) * mm, "end": v(0.1, 0.13) * mm});
            skLineSegment(sketch, "E243", {"start": v(0.1, 0.13) * mm, "end": v(0.08, 0.13) * mm});
            skLineSegment(sketch, "E244", {"start": v(0.08, 0.13) * mm, "end": v(0.07, 0.13) * mm});
            skLineSegment(sketch, "E245", {"start": v(0.07, 0.13) * mm, "end": v(0.05, 0.15) * mm});
            skLineSegment(sketch, "E246", {"start": v(0.05, 0.15) * mm, "end": v(0.04, 0.15) * mm});
            skLineSegment(sketch, "E247", {"start": v(0.04, 0.15) * mm, "end": v(0.04, 0.15) * mm});
            skLineSegment(sketch, "E248", {"start": v(0.04, 0.15) * mm, "end": v(0.03, 0.16) * mm});
            skLineSegment(sketch, "E249", {"start": v(0.03, 0.16) * mm, "end": v(0.03, 0.16) * mm});
            skLineSegment(sketch, "E250", {"start": v(0.03, 0.16) * mm, "end": v(0.02, 0.17) * mm});
            skLineSegment(sketch, "E251", {"start": v(0.02, 0.17) * mm, "end": v(0.02, 0.17) * mm});
            skLineSegment(sketch, "E252", {"start": v(0.02, 0.17) * mm, "end": v(-0.02, 0.18) * mm});
            skLineSegment(sketch, "E253", {"start": v(-0.02, 0.18) * mm, "end": v(-0.03, 0.18) * mm});
            skLineSegment(sketch, "E254", {"start": v(-0.03, 0.18) * mm, "end": v(-0.04, 0.18) * mm});
            skLineSegment(sketch, "E255", {"start": v(-0.04, 0.18) * mm, "end": v(-0.07, 0.17) * mm});
            skLineSegment(sketch, "E256", {"start": v(-0.07, 0.17) * mm, "end": v(-0.07, 0.17) * mm});
            skLineSegment(sketch, "E257", {"start": v(-0.07, 0.17) * mm, "end": v(-0.07, 0.16) * mm});
            skLineSegment(sketch, "E258", {"start": v(-0.07, 0.16) * mm, "end": v(-0.08, 0.15) * mm});
            skLineSegment(sketch, "E259", {"start": v(-0.08, 0.15) * mm, "end": v(-0.09, 0.14) * mm});
            skLineSegment(sketch, "E260", {"start": v(-0.09, 0.14) * mm, "end": v(-0.09, 0.13) * mm});
            skLineSegment(sketch, "E261", {"start": v(-0.09, 0.13) * mm, "end": v(-0.09, 0.12) * mm});
            skLineSegment(sketch, "E262", {"start": v(-0.09, 0.12) * mm, "end": v(-0.08, 0.1) * mm});
            skLineSegment(sketch, "E263", {"start": v(-0.08, 0.1) * mm, "end": v(-0.07, 0.1) * mm});
            skLineSegment(sketch, "E264", {"start": v(-0.07, 0.1) * mm, "end": v(-0.07, 0.1) * mm});
            skLineSegment(sketch, "E265", {"start": v(-0.07, 0.1) * mm, "end": v(-0.06, 0.1) * mm});
            skLineSegment(sketch, "E266", {"start": v(-0.06, 0.1) * mm, "end": v(-0.02, 0.07) * mm});
            skLineSegment(sketch, "E267", {"start": v(-0.02, 0.07) * mm, "end": v(-0.01, 0.07) * mm});
            skLineSegment(sketch, "E268", {"start": v(-0.01, 0.07) * mm, "end": v(0, 0.07) * mm});
            skLineSegment(sketch, "E269", {"start": v(0, 0.07) * mm, "end": v(0.05, 0.06) * mm});
            skLineSegment(sketch, "E270", {"start": v(0.05, 0.06) * mm, "end": v(0.05, 0.06) * mm});
            skLineSegment(sketch, "E271", {"start": v(0.05, 0.06) * mm, "end": v(0.06, 0.06) * mm});
            skLineSegment(sketch, "E272", {"start": v(0.06, 0.06) * mm, "end": v(0.12, 0.04) * mm});
            skLineSegment(sketch, "E273", {"start": v(0.12, 0.04) * mm, "end": v(0.12, 0.03) * mm});
            skLineSegment(sketch, "E274", {"start": v(0.12, 0.03) * mm, "end": v(0.13, 0.03) * mm});
            skLineSegment(sketch, "E275", {"start": v(0.13, 0.03) * mm, "end": v(0.15, 0.01) * mm});
            skLineSegment(sketch, "E276", {"start": v(0.15, 0.01) * mm, "end": v(0.17, -0.01) * mm});
            skLineSegment(sketch, "E277", {"start": v(0.17, -0.01) * mm, "end": v(0.18, -0.02) * mm});
            skLineSegment(sketch, "E278", {"start": v(0.18, -0.02) * mm, "end": v(0.18, -0.03) * mm});
            skLineSegment(sketch, "E279", {"start": v(0.18, -0.03) * mm, "end": v(0.2, -0.06) * mm});
            skLineSegment(sketch, "E280", {"start": v(0.2, -0.06) * mm, "end": v(0.2, -0.1) * mm});
            skLineSegment(sketch, "E281", {"start": v(0.2, -0.1) * mm, "end": v(0.2, -0.11) * mm});
            skLineSegment(sketch, "E282", {"start": v(0.2, -0.11) * mm, "end": v(0.2, -0.12) * mm});
            skLineSegment(sketch, "E283", {"start": v(0.2, -0.12) * mm, "end": v(0.2, -0.16) * mm});
            skLineSegment(sketch, "E284", {"start": v(0.2, -0.16) * mm, "end": v(0.18, -0.2) * mm});
            skLineSegment(sketch, "E285", {"start": v(0.18, -0.2) * mm, "end": v(0.18, -0.2) * mm});
            skLineSegment(sketch, "E286", {"start": v(0.18, -0.2) * mm, "end": v(0.17, -0.21) * mm});
            skLineSegment(sketch, "E287", {"start": v(0.17, -0.21) * mm, "end": v(0.15, -0.24) * mm});
            skLineSegment(sketch, "E288", {"start": v(0.15, -0.24) * mm, "end": v(0.13, -0.27) * mm});
            skLineSegment(sketch, "E289", {"start": v(0.13, -0.27) * mm, "end": v(0.12, -0.27) * mm});
            skLineSegment(sketch, "E290", {"start": v(0.12, -0.27) * mm, "end": v(0.1, -0.28) * mm});
            skLineSegment(sketch, "E291", {"start": v(0.1, -0.28) * mm, "end": v(0.05, -0.3) * mm});
            skLineSegment(sketch, "E292", {"start": v(0.05, -0.3) * mm, "end": v(0, -0.31) * mm});
            skLineSegment(sketch, "E293", {"start": v(0, -0.31) * mm, "end": v(-0.02, -0.31) * mm});
            skLineSegment(sketch, "E294", {"start": v(-0.02, -0.31) * mm, "end": v(-0.04, -0.31) * mm});
            skLineSegment(sketch, "E295", {"start": v(-0.04, -0.31) * mm, "end": v(-0.1, -0.3) * mm});
            skLineSegment(sketch, "E296", {"start": v(-0.1, -0.3) * mm, "end": v(-0.1, -0.3) * mm});
            skLineSegment(sketch, "E297", {"start": v(-0.1, -0.3) * mm, "end": v(-0.15, -0.28) * mm});
            skLineSegment(sketch, "E298", {"start": v(-0.15, -0.28) * mm, "end": v(-0.16, -0.28) * mm});
            skLineSegment(sketch, "E299", {"start": v(-0.16, -0.28) * mm, "end": v(-0.16, -0.28) * mm});
            skLineSegment(sketch, "E300", {"start": v(-0.16, -0.28) * mm, "end": v(-0.2, -0.25) * mm});
            skLineSegment(sketch, "E301", {"start": v(-0.2, -0.25) * mm, "end": v(-0.21, -0.23) * mm});
            skLineSegment(sketch, "E302", {"start": v(-0.21, -0.23) * mm, "end": v(-0.22, -0.23) * mm});
            skLineSegment(sketch, "E303", {"start": v(-0.22, -0.23) * mm, "end": v(-0.22, -0.22) * mm});
            skLineSegment(sketch, "E304", {"start": v(0.3, 0.3) * mm, "end": v(0.77, 0.3) * mm});
            skLineSegment(sketch, "E305", {"start": v(0.77, 0.3) * mm, "end": v(0.78, 0.3) * mm});
            skLineSegment(sketch, "E306", {"start": v(0.78, 0.3) * mm, "end": v(0.8, 0.3) * mm});
            skLineSegment(sketch, "E307", {"start": v(0.8, 0.3) * mm, "end": v(0.8, 0.3) * mm});
            skLineSegment(sketch, "E308", {"start": v(0.8, 0.3) * mm, "end": v(0.81, 0.3) * mm});
            skLineSegment(sketch, "E309", {"start": v(0.81, 0.3) * mm, "end": v(0.82, 0.28) * mm});
            skLineSegment(sketch, "E310", {"start": v(0.82, 0.28) * mm, "end": v(0.83, 0.28) * mm});
            skLineSegment(sketch, "E311", {"start": v(0.83, 0.28) * mm, "end": v(0.83, 0.28) * mm});
            skLineSegment(sketch, "E312", {"start": v(0.83, 0.28) * mm, "end": v(0.83, 0.25) * mm});
            skLineSegment(sketch, "E313", {"start": v(0.83, 0.25) * mm, "end": v(0.83, 0.25) * mm});
            skLineSegment(sketch, "E314", {"start": v(0.83, 0.25) * mm, "end": v(0.83, 0.24) * mm});
            skLineSegment(sketch, "E315", {"start": v(0.83, 0.24) * mm, "end": v(0.83, 0.21) * mm});
            skLineSegment(sketch, "E316", {"start": v(0.83, 0.21) * mm, "end": v(0.83, 0.21) * mm});
            skLineSegment(sketch, "E317", {"start": v(0.83, 0.21) * mm, "end": v(0.82, 0.2) * mm});
            skLineSegment(sketch, "E318", {"start": v(0.82, 0.2) * mm, "end": v(0.81, 0.2) * mm});
            skLineSegment(sketch, "E319", {"start": v(0.81, 0.2) * mm, "end": v(0.81, 0.2) * mm});
            skLineSegment(sketch, "E320", {"start": v(0.81, 0.2) * mm, "end": v(0.8, 0.2) * mm});
            skLineSegment(sketch, "E321", {"start": v(0.8, 0.2) * mm, "end": v(0.78, 0.19) * mm});
            skLineSegment(sketch, "E322", {"start": v(0.78, 0.19) * mm, "end": v(0.77, 0.19) * mm});
            skLineSegment(sketch, "E323", {"start": v(0.77, 0.19) * mm, "end": v(0.6, 0.19) * mm});
            skLineSegment(sketch, "E324", {"start": v(0.6, 0.19) * mm, "end": v(0.6, -0.23) * mm});
            skLineSegment(sketch, "E325", {"start": v(0.6, -0.23) * mm, "end": v(0.6, -0.24) * mm});
            skLineSegment(sketch, "E326", {"start": v(0.6, -0.24) * mm, "end": v(0.6, -0.26) * mm});
            skLineSegment(sketch, "E327", {"start": v(0.6, -0.26) * mm, "end": v(0.6, -0.26) * mm});
            skLineSegment(sketch, "E328", {"start": v(0.6, -0.26) * mm, "end": v(0.6, -0.28) * mm});
            skLineSegment(sketch, "E329", {"start": v(0.6, -0.28) * mm, "end": v(0.6, -0.28) * mm});
            skLineSegment(sketch, "E330", {"start": v(0.6, -0.28) * mm, "end": v(0.6, -0.29) * mm});
            skLineSegment(sketch, "E331", {"start": v(0.6, -0.29) * mm, "end": v(0.58, -0.3) * mm});
            skLineSegment(sketch, "E332", {"start": v(0.58, -0.3) * mm, "end": v(0.58, -0.3) * mm});
            skLineSegment(sketch, "E333", {"start": v(0.58, -0.3) * mm, "end": v(0.55, -0.3) * mm});
            skLineSegment(sketch, "E334", {"start": v(0.55, -0.3) * mm, "end": v(0.54, -0.3) * mm});
            skLineSegment(sketch, "E335", {"start": v(0.54, -0.3) * mm, "end": v(0.53, -0.3) * mm});
            skLineSegment(sketch, "E336", {"start": v(0.53, -0.3) * mm, "end": v(0.5, -0.3) * mm});
            skLineSegment(sketch, "E337", {"start": v(0.5, -0.3) * mm, "end": v(0.5, -0.3) * mm});
            skLineSegment(sketch, "E338", {"start": v(0.5, -0.3) * mm, "end": v(0.48, -0.29) * mm});
            skLineSegment(sketch, "E339", {"start": v(0.48, -0.29) * mm, "end": v(0.47, -0.28) * mm});
            skLineSegment(sketch, "E340", {"start": v(0.47, -0.28) * mm, "end": v(0.47, -0.28) * mm});
            skLineSegment(sketch, "E341", {"start": v(0.47, -0.28) * mm, "end": v(0.47, -0.26) * mm});
            skLineSegment(sketch, "E342", {"start": v(0.47, -0.26) * mm, "end": v(0.47, -0.26) * mm});
            skLineSegment(sketch, "E343", {"start": v(0.47, -0.26) * mm, "end": v(0.47, -0.24) * mm});
            skLineSegment(sketch, "E344", {"start": v(0.47, -0.24) * mm, "end": v(0.47, -0.23) * mm});
            skLineSegment(sketch, "E345", {"start": v(0.47, -0.23) * mm, "end": v(0.47, 0.19) * mm});
            skLineSegment(sketch, "E346", {"start": v(0.47, 0.19) * mm, "end": v(0.3, 0.19) * mm});
            skLineSegment(sketch, "E347", {"start": v(0.3, 0.19) * mm, "end": v(0.3, 0.19) * mm});
            skLineSegment(sketch, "E348", {"start": v(0.3, 0.19) * mm, "end": v(0.27, 0.2) * mm});
            skLineSegment(sketch, "E349", {"start": v(0.27, 0.2) * mm, "end": v(0.27, 0.2) * mm});
            skLineSegment(sketch, "E350", {"start": v(0.27, 0.2) * mm, "end": v(0.26, 0.2) * mm});
            skLineSegment(sketch, "E351", {"start": v(0.26, 0.2) * mm, "end": v(0.25, 0.2) * mm});
            skLineSegment(sketch, "E352", {"start": v(0.25, 0.2) * mm, "end": v(0.25, 0.21) * mm});
            skLineSegment(sketch, "E353", {"start": v(0.25, 0.21) * mm, "end": v(0.25, 0.21) * mm});
            skLineSegment(sketch, "E354", {"start": v(0.25, 0.21) * mm, "end": v(0.25, 0.24) * mm});
            skLineSegment(sketch, "E355", {"start": v(0.25, 0.24) * mm, "end": v(0.25, 0.25) * mm});
            skLineSegment(sketch, "E356", {"start": v(0.25, 0.25) * mm, "end": v(0.25, 0.25) * mm});
            skLineSegment(sketch, "E357", {"start": v(0.25, 0.25) * mm, "end": v(0.25, 0.28) * mm});
            skLineSegment(sketch, "E358", {"start": v(0.25, 0.28) * mm, "end": v(0.25, 0.28) * mm});
            skLineSegment(sketch, "E359", {"start": v(0.25, 0.28) * mm, "end": v(0.26, 0.3) * mm});
            skLineSegment(sketch, "E360", {"start": v(0.26, 0.3) * mm, "end": v(0.26, 0.3) * mm});
            skLineSegment(sketch, "E361", {"start": v(0.26, 0.3) * mm, "end": v(0.27, 0.3) * mm});
            skLineSegment(sketch, "E362", {"start": v(0.27, 0.3) * mm, "end": v(0.3, 0.3) * mm});
            skLineSegment(sketch, "E363", {"start": v(0.3, 0.3) * mm, "end": v(0.3, 0.3) * mm});
            skLineSegment(sketch, "E364", {"start": v(0.98, 0) * mm, "end": v(0.98, -0.02) * mm});
            skLineSegment(sketch, "E365", {"start": v(0.98, -0.02) * mm, "end": v(1, -0.07) * mm});
            skLineSegment(sketch, "E366", {"start": v(1, -0.07) * mm, "end": v(1.02, -0.11) * mm});
            skLineSegment(sketch, "E367", {"start": v(1.02, -0.11) * mm, "end": v(1.03, -0.12) * mm});
            skLineSegment(sketch, "E368", {"start": v(1.03, -0.12) * mm, "end": v(1.04, -0.13) * mm});
            skLineSegment(sketch, "E369", {"start": v(1.04, -0.13) * mm, "end": v(1.08, -0.16) * mm});
            skLineSegment(sketch, "E370", {"start": v(1.08, -0.16) * mm, "end": v(1.13, -0.17) * mm});
            skLineSegment(sketch, "E371", {"start": v(1.13, -0.17) * mm, "end": v(1.14, -0.17) * mm});
            skLineSegment(sketch, "E372", {"start": v(1.14, -0.17) * mm, "end": v(1.15, -0.17) * mm});
            skLineSegment(sketch, "E373", {"start": v(1.15, -0.17) * mm, "end": v(1.2, -0.16) * mm});
            skLineSegment(sketch, "E374", {"start": v(1.2, -0.16) * mm, "end": v(1.24, -0.13) * mm});
            skLineSegment(sketch, "E375", {"start": v(1.24, -0.13) * mm, "end": v(1.25, -0.12) * mm});
            skLineSegment(sketch, "E376", {"start": v(1.25, -0.12) * mm, "end": v(1.25, -0.12) * mm});
            skLineSegment(sketch, "E377", {"start": v(1.25, -0.12) * mm, "end": v(1.28, -0.07) * mm});
            skLineSegment(sketch, "E378", {"start": v(1.28, -0.07) * mm, "end": v(1.3, -0.02) * mm});
            skLineSegment(sketch, "E379", {"start": v(1.3, -0.02) * mm, "end": v(1.3, 0) * mm});
            skLineSegment(sketch, "E380", {"start": v(1.3, 0) * mm, "end": v(1.3, 0.01) * mm});
            skLineSegment(sketch, "E381", {"start": v(1.3, 0.01) * mm, "end": v(1.28, 0.07) * mm});
            skLineSegment(sketch, "E382", {"start": v(1.28, 0.07) * mm, "end": v(1.25, 0.11) * mm});
            skLineSegment(sketch, "E383", {"start": v(1.25, 0.11) * mm, "end": v(1.25, 0.12) * mm});
            skLineSegment(sketch, "E384", {"start": v(1.25, 0.12) * mm, "end": v(1.24, 0.13) * mm});
            skLineSegment(sketch, "E385", {"start": v(1.24, 0.13) * mm, "end": v(1.2, 0.15) * mm});
            skLineSegment(sketch, "E386", {"start": v(1.2, 0.15) * mm, "end": v(1.15, 0.17) * mm});
            skLineSegment(sketch, "E387", {"start": v(1.15, 0.17) * mm, "end": v(1.14, 0.17) * mm});
            skLineSegment(sketch, "E388", {"start": v(1.14, 0.17) * mm, "end": v(1.12, 0.17) * mm});
            skLineSegment(sketch, "E389", {"start": v(1.12, 0.17) * mm, "end": v(1.08, 0.15) * mm});
            skLineSegment(sketch, "E390", {"start": v(1.08, 0.15) * mm, "end": v(1.04, 0.13) * mm});
            skLineSegment(sketch, "E391", {"start": v(1.04, 0.13) * mm, "end": v(1.03, 0.12) * mm});
            skLineSegment(sketch, "E392", {"start": v(1.03, 0.12) * mm, "end": v(1.02, 0.11) * mm});
            skLineSegment(sketch, "E393", {"start": v(1.02, 0.11) * mm, "end": v(1, 0.07) * mm});
            skLineSegment(sketch, "E394", {"start": v(1, 0.07) * mm, "end": v(0.98, 0.02) * mm});
            skLineSegment(sketch, "E395", {"start": v(0.98, 0.02) * mm, "end": v(0.98, 0) * mm});
            skLineSegment(sketch, "E396", {"start": v(1.14, 0.31) * mm, "end": v(1.15, 0.31) * mm});
            skLineSegment(sketch, "E397", {"start": v(1.15, 0.31) * mm, "end": v(1.2, 0.3) * mm});
            skLineSegment(sketch, "E398", {"start": v(1.2, 0.3) * mm, "end": v(1.25, 0.3) * mm});
            skLineSegment(sketch, "E399", {"start": v(1.25, 0.3) * mm, "end": v(1.3, 0.26) * mm});
            skLineSegment(sketch, "E400", {"start": v(1.3, 0.26) * mm, "end": v(1.34, 0.23) * mm});
            skLineSegment(sketch, "E401", {"start": v(1.34, 0.23) * mm, "end": v(1.35, 0.22) * mm});
            skLineSegment(sketch, "E402", {"start": v(1.35, 0.22) * mm, "end": v(1.36, 0.21) * mm});
            skLineSegment(sketch, "E403", {"start": v(1.36, 0.21) * mm, "end": v(1.39, 0.18) * mm});
            skLineSegment(sketch, "E404", {"start": v(1.39, 0.18) * mm, "end": v(1.42, 0.12) * mm});
            skLineSegment(sketch, "E405", {"start": v(1.42, 0.12) * mm, "end": v(1.44, 0.07) * mm});
            skLineSegment(sketch, "E406", {"start": v(1.44, 0.07) * mm, "end": v(1.44, 0.02) * mm});
            skLineSegment(sketch, "E407", {"start": v(1.44, 0.02) * mm, "end": v(1.44, 0) * mm});
            skLineSegment(sketch, "E408", {"start": v(1.44, 0) * mm, "end": v(1.44, -0.03) * mm});
            skLineSegment(sketch, "E409", {"start": v(1.44, -0.03) * mm, "end": v(1.42, -0.12) * mm});
            skLineSegment(sketch, "E410", {"start": v(1.42, -0.12) * mm, "end": v(1.37, -0.2) * mm});
            skLineSegment(sketch, "E411", {"start": v(1.37, -0.2) * mm, "end": v(1.35, -0.22) * mm});
            skLineSegment(sketch, "E412", {"start": v(1.35, -0.22) * mm, "end": v(1.34, -0.23) * mm});
            skLineSegment(sketch, "E413", {"start": v(1.34, -0.23) * mm, "end": v(1.3, -0.26) * mm});
            skLineSegment(sketch, "E414", {"start": v(1.3, -0.26) * mm, "end": v(1.26, -0.3) * mm});
            skLineSegment(sketch, "E415", {"start": v(1.26, -0.3) * mm, "end": v(1.2, -0.3) * mm});
            skLineSegment(sketch, "E416", {"start": v(1.2, -0.3) * mm, "end": v(1.16, -0.32) * mm});
            skLineSegment(sketch, "E417", {"start": v(1.16, -0.32) * mm, "end": v(1.14, -0.32) * mm});
            skLineSegment(sketch, "E418", {"start": v(1.14, -0.32) * mm, "end": v(1.13, -0.32) * mm});
            skLineSegment(sketch, "E419", {"start": v(1.13, -0.32) * mm, "end": v(1.08, -0.3) * mm});
            skLineSegment(sketch, "E420", {"start": v(1.08, -0.3) * mm, "end": v(1.02, -0.3) * mm});
            skLineSegment(sketch, "E421", {"start": v(1.02, -0.3) * mm, "end": v(0.97, -0.26) * mm});
            skLineSegment(sketch, "E422", {"start": v(0.97, -0.26) * mm, "end": v(0.94, -0.23) * mm});
            skLineSegment(sketch, "E423", {"start": v(0.94, -0.23) * mm, "end": v(0.93, -0.22) * mm});
            skLineSegment(sketch, "E424", {"start": v(0.93, -0.22) * mm, "end": v(0.91, -0.21) * mm});
            skLineSegment(sketch, "E425", {"start": v(0.91, -0.21) * mm, "end": v(0.89, -0.18) * mm});
            skLineSegment(sketch, "E426", {"start": v(0.89, -0.18) * mm, "end": v(0.86, -0.12) * mm});
            skLineSegment(sketch, "E427", {"start": v(0.86, -0.12) * mm, "end": v(0.84, -0.07) * mm});
            skLineSegment(sketch, "E428", {"start": v(0.84, -0.07) * mm, "end": v(0.84, -0.02) * mm});
            skLineSegment(sketch, "E429", {"start": v(0.84, -0.02) * mm, "end": v(0.84, 0) * mm});
            skLineSegment(sketch, "E430", {"start": v(0.84, 0) * mm, "end": v(0.84, 0.01) * mm});
            skLineSegment(sketch, "E431", {"start": v(0.84, 0.01) * mm, "end": v(0.84, 0.06) * mm});
            skLineSegment(sketch, "E432", {"start": v(0.84, 0.06) * mm, "end": v(0.86, 0.11) * mm});
            skLineSegment(sketch, "E433", {"start": v(0.86, 0.11) * mm, "end": v(0.86, 0.12) * mm});
            skLineSegment(sketch, "E434", {"start": v(0.86, 0.12) * mm, "end": v(0.87, 0.13) * mm});
            skLineSegment(sketch, "E435", {"start": v(0.87, 0.13) * mm, "end": v(0.9, 0.18) * mm});
            skLineSegment(sketch, "E436", {"start": v(0.9, 0.18) * mm, "end": v(0.92, 0.22) * mm});
            skLineSegment(sketch, "E437", {"start": v(0.92, 0.22) * mm, "end": v(0.93, 0.23) * mm});
            skLineSegment(sketch, "E438", {"start": v(0.93, 0.23) * mm, "end": v(0.94, 0.23) * mm});
            skLineSegment(sketch, "E439", {"start": v(0.94, 0.23) * mm, "end": v(0.97, 0.26) * mm});
            skLineSegment(sketch, "E440", {"start": v(0.97, 0.26) * mm, "end": v(1.02, 0.29) * mm});
            skLineSegment(sketch, "E441", {"start": v(1.02, 0.29) * mm, "end": v(1.02, 0.29) * mm});
            skLineSegment(sketch, "E442", {"start": v(1.02, 0.29) * mm, "end": v(1.03, 0.3) * mm});
            skLineSegment(sketch, "E443", {"start": v(1.03, 0.3) * mm, "end": v(1.11, 0.31) * mm});
            skLineSegment(sketch, "E444", {"start": v(1.11, 0.31) * mm, "end": v(1.14, 0.31) * mm});
            skSolve(sketch);
        }
        {
            var Q0;
            Q0 = qSketchRegion(id + "F7", true);
            extrude(context, id + "F8", {"entities" : qUnion([Q0]), "depth" : 0.5 * mm, "offsetDistance" : 25 * mm});
        }
        {
            var Q0;
            Q0=makeQuery(id+"F8.opExtrude","SWEPT_BODY",BODY,{"disambiguationData":[OSD([sQuery(id+"F7.wireOp",EDGE,"E15"),sQuery(id+"F7.wireOp",EDGE,"E16"),sQuery(id+"F7.wireOp",EDGE,"E17"),sQuery(id+"F7.wireOp",EDGE,"E18"),sQuery(id+"F7.wireOp",EDGE,"E19"),sQuery(id+"F7.wireOp",EDGE,"E20"),sQuery(id+"F7.wireOp",EDGE,"E21"),sQuery(id+"F7.wireOp",EDGE,"E22"),sQuery(id+"F7.wireOp",EDGE,"E23"),sQuery(id+"F7.wireOp",EDGE,"E24"),sQuery(id+"F7.wireOp",EDGE,"E25"),sQuery(id+"F7.wireOp",EDGE,"E26"),sQuery(id+"F7.wireOp",EDGE,"E27"),sQuery(id+"F7.wireOp",EDGE,"E28"),sQuery(id+"F7.wireOp",EDGE,"E29"),sQuery(id+"F7.wireOp",EDGE,"E29"),sQuery(id+"F7.wireOp",EDGE,"E30"),sQuery(id+"F7.wireOp",EDGE,"E31"),sQuery(id+"F7.wireOp",EDGE,"E32"),sQuery(id+"F7.wireOp",EDGE,"E33"),sQuery(id+"F7.wireOp",EDGE,"E34"),sQuery(id+"F7.wireOp",EDGE,"E35"),sQuery(id+"F7.wireOp",EDGE,"E35"),sQuery(id+"F7.wireOp",EDGE,"E36"),sQuery(id+"F7.wireOp",EDGE,"E37"),sQuery(id+"F7.wireOp",EDGE,"E38"),sQuery(id+"F7.wireOp",EDGE,"E39"),sQuery(id+"F7.wireOp",EDGE,"E40"),sQuery(id+"F7.wireOp",EDGE,"E41"),sQuery(id+"F7.wireOp",EDGE,"E42"),sQuery(id+"F7.wireOp",EDGE,"E43"),sQuery(id+"F7.wireOp",EDGE,"E44"),sQuery(id+"F7.wireOp",EDGE,"E45"),sQuery(id+"F7.wireOp",EDGE,"E46"),sQuery(id+"F7.wireOp",EDGE,"E47"),sQuery(id+"F7.wireOp",EDGE,"E48"),sQuery(id+"F7.wireOp",EDGE,"E49"),sQuery(id+"F7.wireOp",EDGE,"E50"),sQuery(id+"F7.wireOp",EDGE,"E51"),sQuery(id+"F7.wireOp",EDGE,"E52"),sQuery(id+"F7.wireOp",EDGE,"E53"),sQuery(id+"F7.wireOp",EDGE,"E54"),sQuery(id+"F7.wireOp",EDGE,"E55"),sQuery(id+"F7.wireOp",EDGE,"E56"),sQuery(id+"F7.wireOp",EDGE,"E57"),sQuery(id+"F7.wireOp",EDGE,"E57"),sQuery(id+"F7.wireOp",EDGE,"E58"),sQuery(id+"F7.wireOp",EDGE,"E59"),sQuery(id+"F7.wireOp",EDGE,"E60"),sQuery(id+"F7.wireOp",EDGE,"E61"),sQuery(id+"F7.wireOp",EDGE,"E62"),sQuery(id+"F7.wireOp",EDGE,"E63"),sQuery(id+"F7.wireOp",EDGE,"E64"),sQuery(id+"F7.wireOp",EDGE,"E65"),sQuery(id+"F7.wireOp",EDGE,"E66"),sQuery(id+"F7.wireOp",EDGE,"E67"),sQuery(id+"F7.wireOp",EDGE,"E68"),sQuery(id+"F7.wireOp",EDGE,"E69"),sQuery(id+"F7.wireOp",EDGE,"E70"),sQuery(id+"F7.wireOp",EDGE,"E70"),sQuery(id+"F7.wireOp",EDGE,"E71"),sQuery(id+"F7.wireOp",EDGE,"E72"),sQuery(id+"F7.wireOp",EDGE,"E73"),sQuery(id+"F7.wireOp",EDGE,"E74"),sQuery(id+"F7.wireOp",EDGE,"E75"),sQuery(id+"F7.wireOp",EDGE,"E76"),sQuery(id+"F7.wireOp",EDGE,"E76"),sQuery(id+"F7.wireOp",EDGE,"E77"),sQuery(id+"F7.wireOp",EDGE,"E78"),sQuery(id+"F7.wireOp",EDGE,"E79"),sQuery(id+"F7.wireOp",EDGE,"E80"),sQuery(id+"F7.wireOp",EDGE,"E81"),sQuery(id+"F7.wireOp",EDGE,"E82"),sQuery(id+"F7.wireOp",EDGE,"E83"),sQuery(id+"F7.wireOp",EDGE,"E84"),sQuery(id+"F7.wireOp",EDGE,"E84"),sQuery(id+"F7.wireOp",EDGE,"E85"),sQuery(id+"F7.wireOp",EDGE,"E86"),sQuery(id+"F7.wireOp",EDGE,"E87"),sQuery(id+"F7.wireOp",EDGE,"E88"),sQuery(id+"F7.wireOp",EDGE,"E89"),sQuery(id+"F7.wireOp",EDGE,"E90"),sQuery(id+"F7.wireOp",EDGE,"E91"),sQuery(id+"F7.wireOp",EDGE,"E92"),sQuery(id+"F7.wireOp",EDGE,"E93"),sQuery(id+"F7.wireOp",EDGE,"E94"),sQuery(id+"F7.wireOp",EDGE,"E95"),sQuery(id+"F7.wireOp",EDGE,"E96"),sQuery(id+"F7.wireOp",EDGE,"E97"),sQuery(id+"F7.wireOp",EDGE,"E98"),sQuery(id+"F7.wireOp",EDGE,"E99"),sQuery(id+"F7.wireOp",EDGE,"E15")])]});
            var Q1;
            Q1=makeQuery(id+"F8.opExtrude","SWEPT_BODY",BODY,{"disambiguationData":[OSD([sQuery(id+"F7.wireOp",EDGE,"E100"),sQuery(id+"F7.wireOp",EDGE,"E101"),sQuery(id+"F7.wireOp",EDGE,"E102"),sQuery(id+"F7.wireOp",EDGE,"E103"),sQuery(id+"F7.wireOp",EDGE,"E103"),sQuery(id+"F7.wireOp",EDGE,"E104"),sQuery(id+"F7.wireOp",EDGE,"E105"),sQuery(id+"F7.wireOp",EDGE,"E106"),sQuery(id+"F7.wireOp",EDGE,"E107"),sQuery(id+"F7.wireOp",EDGE,"E108"),sQuery(id+"F7.wireOp",EDGE,"E109"),sQuery(id+"F7.wireOp",EDGE,"E110"),sQuery(id+"F7.wireOp",EDGE,"E111"),sQuery(id+"F7.wireOp",EDGE,"E112"),sQuery(id+"F7.wireOp",EDGE,"E113"),sQuery(id+"F7.wireOp",EDGE,"E114"),sQuery(id+"F7.wireOp",EDGE,"E115"),sQuery(id+"F7.wireOp",EDGE,"E116"),sQuery(id+"F7.wireOp",EDGE,"E117"),sQuery(id+"F7.wireOp",EDGE,"E118"),sQuery(id+"F7.wireOp",EDGE,"E119"),sQuery(id+"F7.wireOp",EDGE,"E120"),sQuery(id+"F7.wireOp",EDGE,"E121"),sQuery(id+"F7.wireOp",EDGE,"E122"),sQuery(id+"F7.wireOp",EDGE,"E123"),sQuery(id+"F7.wireOp",EDGE,"E124"),sQuery(id+"F7.wireOp",EDGE,"E125"),sQuery(id+"F7.wireOp",EDGE,"E126"),sQuery(id+"F7.wireOp",EDGE,"E127"),sQuery(id+"F7.wireOp",EDGE,"E128"),sQuery(id+"F7.wireOp",EDGE,"E129"),sQuery(id+"F7.wireOp",EDGE,"E130"),sQuery(id+"F7.wireOp",EDGE,"E131"),sQuery(id+"F7.wireOp",EDGE,"E132"),sQuery(id+"F7.wireOp",EDGE,"E133"),sQuery(id+"F7.wireOp",EDGE,"E134"),sQuery(id+"F7.wireOp",EDGE,"E135"),sQuery(id+"F7.wireOp",EDGE,"E136"),sQuery(id+"F7.wireOp",EDGE,"E137"),sQuery(id+"F7.wireOp",EDGE,"E137"),sQuery(id+"F7.wireOp",EDGE,"E138"),sQuery(id+"F7.wireOp",EDGE,"E139"),sQuery(id+"F7.wireOp",EDGE,"E140"),sQuery(id+"F7.wireOp",EDGE,"E141"),sQuery(id+"F7.wireOp",EDGE,"E142"),sQuery(id+"F7.wireOp",EDGE,"E143"),sQuery(id+"F7.wireOp",EDGE,"E144"),sQuery(id+"F7.wireOp",EDGE,"E145"),sQuery(id+"F7.wireOp",EDGE,"E146"),sQuery(id+"F7.wireOp",EDGE,"E147"),sQuery(id+"F7.wireOp",EDGE,"E148"),sQuery(id+"F7.wireOp",EDGE,"E149"),sQuery(id+"F7.wireOp",EDGE,"E150"),sQuery(id+"F7.wireOp",EDGE,"E151"),sQuery(id+"F7.wireOp",EDGE,"E152"),sQuery(id+"F7.wireOp",EDGE,"E153"),sQuery(id+"F7.wireOp",EDGE,"E154"),sQuery(id+"F7.wireOp",EDGE,"E155"),sQuery(id+"F7.wireOp",EDGE,"E156"),sQuery(id+"F7.wireOp",EDGE,"E156"),sQuery(id+"F7.wireOp",EDGE,"E157"),sQuery(id+"F7.wireOp",EDGE,"E158"),sQuery(id+"F7.wireOp",EDGE,"E159"),sQuery(id+"F7.wireOp",EDGE,"E160"),sQuery(id+"F7.wireOp",EDGE,"E161"),sQuery(id+"F7.wireOp",EDGE,"E162"),sQuery(id+"F7.wireOp",EDGE,"E163"),sQuery(id+"F7.wireOp",EDGE,"E164"),sQuery(id+"F7.wireOp",EDGE,"E165"),sQuery(id+"F7.wireOp",EDGE,"E166"),sQuery(id+"F7.wireOp",EDGE,"E167"),sQuery(id+"F7.wireOp",EDGE,"E168"),sQuery(id+"F7.wireOp",EDGE,"E169"),sQuery(id+"F7.wireOp",EDGE,"E170"),sQuery(id+"F7.wireOp",EDGE,"E171")])]});
            var Q2;
            Q2=makeQuery(id+"F8.opExtrude","SWEPT_BODY",BODY,{"disambiguationData":[OSD([sQuery(id+"F7.wireOp",EDGE,"E172"),sQuery(id+"F7.wireOp",EDGE,"E173"),sQuery(id+"F7.wireOp",EDGE,"E174"),sQuery(id+"F7.wireOp",EDGE,"E175"),sQuery(id+"F7.wireOp",EDGE,"E176"),sQuery(id+"F7.wireOp",EDGE,"E177"),sQuery(id+"F7.wireOp",EDGE,"E178"),sQuery(id+"F7.wireOp",EDGE,"E179"),sQuery(id+"F7.wireOp",EDGE,"E180"),sQuery(id+"F7.wireOp",EDGE,"E181"),sQuery(id+"F7.wireOp",EDGE,"E182"),sQuery(id+"F7.wireOp",EDGE,"E183"),sQuery(id+"F7.wireOp",EDGE,"E184"),sQuery(id+"F7.wireOp",EDGE,"E185"),sQuery(id+"F7.wireOp",EDGE,"E186"),sQuery(id+"F7.wireOp",EDGE,"E187"),sQuery(id+"F7.wireOp",EDGE,"E188"),sQuery(id+"F7.wireOp",EDGE,"E189"),sQuery(id+"F7.wireOp",EDGE,"E190"),sQuery(id+"F7.wireOp",EDGE,"E191"),sQuery(id+"F7.wireOp",EDGE,"E192"),sQuery(id+"F7.wireOp",EDGE,"E193"),sQuery(id+"F7.wireOp",EDGE,"E194"),sQuery(id+"F7.wireOp",EDGE,"E195"),sQuery(id+"F7.wireOp",EDGE,"E196"),sQuery(id+"F7.wireOp",EDGE,"E197"),sQuery(id+"F7.wireOp",EDGE,"E198"),sQuery(id+"F7.wireOp",EDGE,"E199"),sQuery(id+"F7.wireOp",EDGE,"E200"),sQuery(id+"F7.wireOp",EDGE,"E200"),sQuery(id+"F7.wireOp",EDGE,"E201"),sQuery(id+"F7.wireOp",EDGE,"E202"),sQuery(id+"F7.wireOp",EDGE,"E203"),sQuery(id+"F7.wireOp",EDGE,"E204"),sQuery(id+"F7.wireOp",EDGE,"E205"),sQuery(id+"F7.wireOp",EDGE,"E206"),sQuery(id+"F7.wireOp",EDGE,"E207"),sQuery(id+"F7.wireOp",EDGE,"E208"),sQuery(id+"F7.wireOp",EDGE,"E209"),sQuery(id+"F7.wireOp",EDGE,"E210"),sQuery(id+"F7.wireOp",EDGE,"E211"),sQuery(id+"F7.wireOp",EDGE,"E212"),sQuery(id+"F7.wireOp",EDGE,"E213"),sQuery(id+"F7.wireOp",EDGE,"E214"),sQuery(id+"F7.wireOp",EDGE,"E215"),sQuery(id+"F7.wireOp",EDGE,"E216"),sQuery(id+"F7.wireOp",EDGE,"E217"),sQuery(id+"F7.wireOp",EDGE,"E218"),sQuery(id+"F7.wireOp",EDGE,"E219"),sQuery(id+"F7.wireOp",EDGE,"E220"),sQuery(id+"F7.wireOp",EDGE,"E221"),sQuery(id+"F7.wireOp",EDGE,"E222"),sQuery(id+"F7.wireOp",EDGE,"E223"),sQuery(id+"F7.wireOp",EDGE,"E224"),sQuery(id+"F7.wireOp",EDGE,"E225"),sQuery(id+"F7.wireOp",EDGE,"E226"),sQuery(id+"F7.wireOp",EDGE,"E227"),sQuery(id+"F7.wireOp",EDGE,"E228"),sQuery(id+"F7.wireOp",EDGE,"E229"),sQuery(id+"F7.wireOp",EDGE,"E230"),sQuery(id+"F7.wireOp",EDGE,"E231"),sQuery(id+"F7.wireOp",EDGE,"E232"),sQuery(id+"F7.wireOp",EDGE,"E233"),sQuery(id+"F7.wireOp",EDGE,"E234"),sQuery(id+"F7.wireOp",EDGE,"E235"),sQuery(id+"F7.wireOp",EDGE,"E236"),sQuery(id+"F7.wireOp",EDGE,"E237"),sQuery(id+"F7.wireOp",EDGE,"E238"),sQuery(id+"F7.wireOp",EDGE,"E239"),sQuery(id+"F7.wireOp",EDGE,"E240"),sQuery(id+"F7.wireOp",EDGE,"E241"),sQuery(id+"F7.wireOp",EDGE,"E242"),sQuery(id+"F7.wireOp",EDGE,"E243"),sQuery(id+"F7.wireOp",EDGE,"E244"),sQuery(id+"F7.wireOp",EDGE,"E245"),sQuery(id+"F7.wireOp",EDGE,"E246"),sQuery(id+"F7.wireOp",EDGE,"E247"),sQuery(id+"F7.wireOp",EDGE,"E248"),sQuery(id+"F7.wireOp",EDGE,"E249"),sQuery(id+"F7.wireOp",EDGE,"E249"),sQuery(id+"F7.wireOp",EDGE,"E250"),sQuery(id+"F7.wireOp",EDGE,"E251"),sQuery(id+"F7.wireOp",EDGE,"E251"),sQuery(id+"F7.wireOp",EDGE,"E252"),sQuery(id+"F7.wireOp",EDGE,"E253"),sQuery(id+"F7.wireOp",EDGE,"E254"),sQuery(id+"F7.wireOp",EDGE,"E255"),sQuery(id+"F7.wireOp",EDGE,"E256"),sQuery(id+"F7.wireOp",EDGE,"E257"),sQuery(id+"F7.wireOp",EDGE,"E258"),sQuery(id+"F7.wireOp",EDGE,"E259"),sQuery(id+"F7.wireOp",EDGE,"E260"),sQuery(id+"F7.wireOp",EDGE,"E261"),sQuery(id+"F7.wireOp",EDGE,"E262"),sQuery(id+"F7.wireOp",EDGE,"E263"),sQuery(id+"F7.wireOp",EDGE,"E264"),sQuery(id+"F7.wireOp",EDGE,"E265"),sQuery(id+"F7.wireOp",EDGE,"E266"),sQuery(id+"F7.wireOp",EDGE,"E267"),sQuery(id+"F7.wireOp",EDGE,"E268"),sQuery(id+"F7.wireOp",EDGE,"E269"),sQuery(id+"F7.wireOp",EDGE,"E270"),sQuery(id+"F7.wireOp",EDGE,"E271"),sQuery(id+"F7.wireOp",EDGE,"E272"),sQuery(id+"F7.wireOp",EDGE,"E273"),sQuery(id+"F7.wireOp",EDGE,"E274"),sQuery(id+"F7.wireOp",EDGE,"E275"),sQuery(id+"F7.wireOp",EDGE,"E276"),sQuery(id+"F7.wireOp",EDGE,"E277"),sQuery(id+"F7.wireOp",EDGE,"E278"),sQuery(id+"F7.wireOp",EDGE,"E279"),sQuery(id+"F7.wireOp",EDGE,"E280"),sQuery(id+"F7.wireOp",EDGE,"E281"),sQuery(id+"F7.wireOp",EDGE,"E282"),sQuery(id+"F7.wireOp",EDGE,"E283"),sQuery(id+"F7.wireOp",EDGE,"E284"),sQuery(id+"F7.wireOp",EDGE,"E285"),sQuery(id+"F7.wireOp",EDGE,"E286"),sQuery(id+"F7.wireOp",EDGE,"E287"),sQuery(id+"F7.wireOp",EDGE,"E288"),sQuery(id+"F7.wireOp",EDGE,"E289"),sQuery(id+"F7.wireOp",EDGE,"E290"),sQuery(id+"F7.wireOp",EDGE,"E291"),sQuery(id+"F7.wireOp",EDGE,"E292"),sQuery(id+"F7.wireOp",EDGE,"E293"),sQuery(id+"F7.wireOp",EDGE,"E294"),sQuery(id+"F7.wireOp",EDGE,"E295"),sQuery(id+"F7.wireOp",EDGE,"E296"),sQuery(id+"F7.wireOp",EDGE,"E296"),sQuery(id+"F7.wireOp",EDGE,"E297"),sQuery(id+"F7.wireOp",EDGE,"E298"),sQuery(id+"F7.wireOp",EDGE,"E299"),sQuery(id+"F7.wireOp",EDGE,"E300"),sQuery(id+"F7.wireOp",EDGE,"E301"),sQuery(id+"F7.wireOp",EDGE,"E302"),sQuery(id+"F7.wireOp",EDGE,"E303")])]});
            var Q3;
            Q3=makeQuery(id+"F8.opExtrude","SWEPT_BODY",BODY,{"disambiguationData":[OSD([sQuery(id+"F7.wireOp",EDGE,"E304"),sQuery(id+"F7.wireOp",EDGE,"E305"),sQuery(id+"F7.wireOp",EDGE,"E306"),sQuery(id+"F7.wireOp",EDGE,"E307"),sQuery(id+"F7.wireOp",EDGE,"E308"),sQuery(id+"F7.wireOp",EDGE,"E309"),sQuery(id+"F7.wireOp",EDGE,"E310"),sQuery(id+"F7.wireOp",EDGE,"E311"),sQuery(id+"F7.wireOp",EDGE,"E312"),sQuery(id+"F7.wireOp",EDGE,"E313"),sQuery(id+"F7.wireOp",EDGE,"E314"),sQuery(id+"F7.wireOp",EDGE,"E315"),sQuery(id+"F7.wireOp",EDGE,"E316"),sQuery(id+"F7.wireOp",EDGE,"E317"),sQuery(id+"F7.wireOp",EDGE,"E318"),sQuery(id+"F7.wireOp",EDGE,"E319"),sQuery(id+"F7.wireOp",EDGE,"E320"),sQuery(id+"F7.wireOp",EDGE,"E321"),sQuery(id+"F7.wireOp",EDGE,"E322"),sQuery(id+"F7.wireOp",EDGE,"E323"),sQuery(id+"F7.wireOp",EDGE,"E324"),sQuery(id+"F7.wireOp",EDGE,"E325"),sQuery(id+"F7.wireOp",EDGE,"E326"),sQuery(id+"F7.wireOp",EDGE,"E327"),sQuery(id+"F7.wireOp",EDGE,"E327"),sQuery(id+"F7.wireOp",EDGE,"E328"),sQuery(id+"F7.wireOp",EDGE,"E329"),sQuery(id+"F7.wireOp",EDGE,"E330"),sQuery(id+"F7.wireOp",EDGE,"E331"),sQuery(id+"F7.wireOp",EDGE,"E332"),sQuery(id+"F7.wireOp",EDGE,"E332"),sQuery(id+"F7.wireOp",EDGE,"E333"),sQuery(id+"F7.wireOp",EDGE,"E334"),sQuery(id+"F7.wireOp",EDGE,"E335"),sQuery(id+"F7.wireOp",EDGE,"E336"),sQuery(id+"F7.wireOp",EDGE,"E337"),sQuery(id+"F7.wireOp",EDGE,"E337"),sQuery(id+"F7.wireOp",EDGE,"E338"),sQuery(id+"F7.wireOp",EDGE,"E339"),sQuery(id+"F7.wireOp",EDGE,"E340"),sQuery(id+"F7.wireOp",EDGE,"E341"),sQuery(id+"F7.wireOp",EDGE,"E342"),sQuery(id+"F7.wireOp",EDGE,"E342"),sQuery(id+"F7.wireOp",EDGE,"E343"),sQuery(id+"F7.wireOp",EDGE,"E344"),sQuery(id+"F7.wireOp",EDGE,"E345"),sQuery(id+"F7.wireOp",EDGE,"E346"),sQuery(id+"F7.wireOp",EDGE,"E347"),sQuery(id+"F7.wireOp",EDGE,"E348"),sQuery(id+"F7.wireOp",EDGE,"E349"),sQuery(id+"F7.wireOp",EDGE,"E350"),sQuery(id+"F7.wireOp",EDGE,"E351"),sQuery(id+"F7.wireOp",EDGE,"E352"),sQuery(id+"F7.wireOp",EDGE,"E353"),sQuery(id+"F7.wireOp",EDGE,"E354"),sQuery(id+"F7.wireOp",EDGE,"E355"),sQuery(id+"F7.wireOp",EDGE,"E356"),sQuery(id+"F7.wireOp",EDGE,"E357"),sQuery(id+"F7.wireOp",EDGE,"E358"),sQuery(id+"F7.wireOp",EDGE,"E358"),sQuery(id+"F7.wireOp",EDGE,"E359"),sQuery(id+"F7.wireOp",EDGE,"E360"),sQuery(id+"F7.wireOp",EDGE,"E361"),sQuery(id+"F7.wireOp",EDGE,"E362"),sQuery(id+"F7.wireOp",EDGE,"E363")])]});
            var Q4;
            Q4=makeQuery(id+"F8.opExtrude","SWEPT_BODY",BODY,{"disambiguationData":[OSD([sQuery(id+"F7.wireOp",EDGE,"E364"),sQuery(id+"F7.wireOp",EDGE,"E365"),sQuery(id+"F7.wireOp",EDGE,"E366"),sQuery(id+"F7.wireOp",EDGE,"E367"),sQuery(id+"F7.wireOp",EDGE,"E368"),sQuery(id+"F7.wireOp",EDGE,"E369"),sQuery(id+"F7.wireOp",EDGE,"E370"),sQuery(id+"F7.wireOp",EDGE,"E371"),sQuery(id+"F7.wireOp",EDGE,"E372"),sQuery(id+"F7.wireOp",EDGE,"E373"),sQuery(id+"F7.wireOp",EDGE,"E374"),sQuery(id+"F7.wireOp",EDGE,"E375"),sQuery(id+"F7.wireOp",EDGE,"E376"),sQuery(id+"F7.wireOp",EDGE,"E377"),sQuery(id+"F7.wireOp",EDGE,"E378"),sQuery(id+"F7.wireOp",EDGE,"E379"),sQuery(id+"F7.wireOp",EDGE,"E380"),sQuery(id+"F7.wireOp",EDGE,"E381"),sQuery(id+"F7.wireOp",EDGE,"E382"),sQuery(id+"F7.wireOp",EDGE,"E383"),sQuery(id+"F7.wireOp",EDGE,"E384"),sQuery(id+"F7.wireOp",EDGE,"E385"),sQuery(id+"F7.wireOp",EDGE,"E386"),sQuery(id+"F7.wireOp",EDGE,"E387"),sQuery(id+"F7.wireOp",EDGE,"E388"),sQuery(id+"F7.wireOp",EDGE,"E389"),sQuery(id+"F7.wireOp",EDGE,"E390"),sQuery(id+"F7.wireOp",EDGE,"E391"),sQuery(id+"F7.wireOp",EDGE,"E392"),sQuery(id+"F7.wireOp",EDGE,"E393"),sQuery(id+"F7.wireOp",EDGE,"E394"),sQuery(id+"F7.wireOp",EDGE,"E395"),sQuery(id+"F7.wireOp",EDGE,"E396"),sQuery(id+"F7.wireOp",EDGE,"E397"),sQuery(id+"F7.wireOp",EDGE,"E398"),sQuery(id+"F7.wireOp",EDGE,"E399"),sQuery(id+"F7.wireOp",EDGE,"E400"),sQuery(id+"F7.wireOp",EDGE,"E401"),sQuery(id+"F7.wireOp",EDGE,"E402"),sQuery(id+"F7.wireOp",EDGE,"E403"),sQuery(id+"F7.wireOp",EDGE,"E404"),sQuery(id+"F7.wireOp",EDGE,"E405"),sQuery(id+"F7.wireOp",EDGE,"E406"),sQuery(id+"F7.wireOp",EDGE,"E407"),sQuery(id+"F7.wireOp",EDGE,"E408"),sQuery(id+"F7.wireOp",EDGE,"E409"),sQuery(id+"F7.wireOp",EDGE,"E410"),sQuery(id+"F7.wireOp",EDGE,"E411"),sQuery(id+"F7.wireOp",EDGE,"E412"),sQuery(id+"F7.wireOp",EDGE,"E413"),sQuery(id+"F7.wireOp",EDGE,"E414"),sQuery(id+"F7.wireOp",EDGE,"E415"),sQuery(id+"F7.wireOp",EDGE,"E416"),sQuery(id+"F7.wireOp",EDGE,"E417"),sQuery(id+"F7.wireOp",EDGE,"E418"),sQuery(id+"F7.wireOp",EDGE,"E419"),sQuery(id+"F7.wireOp",EDGE,"E420"),sQuery(id+"F7.wireOp",EDGE,"E421"),sQuery(id+"F7.wireOp",EDGE,"E422"),sQuery(id+"F7.wireOp",EDGE,"E423"),sQuery(id+"F7.wireOp",EDGE,"E424"),sQuery(id+"F7.wireOp",EDGE,"E425"),sQuery(id+"F7.wireOp",EDGE,"E426"),sQuery(id+"F7.wireOp",EDGE,"E427"),sQuery(id+"F7.wireOp",EDGE,"E428"),sQuery(id+"F7.wireOp",EDGE,"E429"),sQuery(id+"F7.wireOp",EDGE,"E430"),sQuery(id+"F7.wireOp",EDGE,"E431"),sQuery(id+"F7.wireOp",EDGE,"E432"),sQuery(id+"F7.wireOp",EDGE,"E433"),sQuery(id+"F7.wireOp",EDGE,"E434"),sQuery(id+"F7.wireOp",EDGE,"E435"),sQuery(id+"F7.wireOp",EDGE,"E436"),sQuery(id+"F7.wireOp",EDGE,"E437"),sQuery(id+"F7.wireOp",EDGE,"E438"),sQuery(id+"F7.wireOp",EDGE,"E439"),sQuery(id+"F7.wireOp",EDGE,"E440"),sQuery(id+"F7.wireOp",EDGE,"E441"),sQuery(id+"F7.wireOp",EDGE,"E442"),sQuery(id+"F7.wireOp",EDGE,"E443"),sQuery(id+"F7.wireOp",EDGE,"E444")])]});
            var Q5;
            Q5=qCreatedBy(makeId("Origin.pointOp"),VERTEX);
            transform(context, id + "F9", {"entities" : qUnion([Q0, Q1, Q2, Q3, Q4]), "transformType" : TransformType.SCALE_UNIFORMLY, "scale" : 24, "scalePoint" : qUnion([Q5]), "makeCopy" : false});
        }
        {
            var Q0;
            Q0=makeQuery(id+"F8.opExtrude","SWEPT_BODY",BODY,{"disambiguationData":[OSD([sQuery(id+"F7.wireOp",EDGE,"E15"),sQuery(id+"F7.wireOp",EDGE,"E16"),sQuery(id+"F7.wireOp",EDGE,"E17"),sQuery(id+"F7.wireOp",EDGE,"E18"),sQuery(id+"F7.wireOp",EDGE,"E19"),sQuery(id+"F7.wireOp",EDGE,"E20"),sQuery(id+"F7.wireOp",EDGE,"E21"),sQuery(id+"F7.wireOp",EDGE,"E22"),sQuery(id+"F7.wireOp",EDGE,"E23"),sQuery(id+"F7.wireOp",EDGE,"E24"),sQuery(id+"F7.wireOp",EDGE,"E25"),sQuery(id+"F7.wireOp",EDGE,"E26"),sQuery(id+"F7.wireOp",EDGE,"E27"),sQuery(id+"F7.wireOp",EDGE,"E28"),sQuery(id+"F7.wireOp",EDGE,"E29"),sQuery(id+"F7.wireOp",EDGE,"E29"),sQuery(id+"F7.wireOp",EDGE,"E30"),sQuery(id+"F7.wireOp",EDGE,"E31"),sQuery(id+"F7.wireOp",EDGE,"E32"),sQuery(id+"F7.wireOp",EDGE,"E33"),sQuery(id+"F7.wireOp",EDGE,"E34"),sQuery(id+"F7.wireOp",EDGE,"E35"),sQuery(id+"F7.wireOp",EDGE,"E35"),sQuery(id+"F7.wireOp",EDGE,"E36"),sQuery(id+"F7.wireOp",EDGE,"E37"),sQuery(id+"F7.wireOp",EDGE,"E38"),sQuery(id+"F7.wireOp",EDGE,"E39"),sQuery(id+"F7.wireOp",EDGE,"E40"),sQuery(id+"F7.wireOp",EDGE,"E41"),sQuery(id+"F7.wireOp",EDGE,"E42"),sQuery(id+"F7.wireOp",EDGE,"E43"),sQuery(id+"F7.wireOp",EDGE,"E44"),sQuery(id+"F7.wireOp",EDGE,"E45"),sQuery(id+"F7.wireOp",EDGE,"E46"),sQuery(id+"F7.wireOp",EDGE,"E47"),sQuery(id+"F7.wireOp",EDGE,"E48"),sQuery(id+"F7.wireOp",EDGE,"E49"),sQuery(id+"F7.wireOp",EDGE,"E50"),sQuery(id+"F7.wireOp",EDGE,"E51"),sQuery(id+"F7.wireOp",EDGE,"E52"),sQuery(id+"F7.wireOp",EDGE,"E53"),sQuery(id+"F7.wireOp",EDGE,"E54"),sQuery(id+"F7.wireOp",EDGE,"E55"),sQuery(id+"F7.wireOp",EDGE,"E56"),sQuery(id+"F7.wireOp",EDGE,"E57"),sQuery(id+"F7.wireOp",EDGE,"E57"),sQuery(id+"F7.wireOp",EDGE,"E58"),sQuery(id+"F7.wireOp",EDGE,"E59"),sQuery(id+"F7.wireOp",EDGE,"E60"),sQuery(id+"F7.wireOp",EDGE,"E61"),sQuery(id+"F7.wireOp",EDGE,"E62"),sQuery(id+"F7.wireOp",EDGE,"E63"),sQuery(id+"F7.wireOp",EDGE,"E64"),sQuery(id+"F7.wireOp",EDGE,"E65"),sQuery(id+"F7.wireOp",EDGE,"E66"),sQuery(id+"F7.wireOp",EDGE,"E67"),sQuery(id+"F7.wireOp",EDGE,"E68"),sQuery(id+"F7.wireOp",EDGE,"E69"),sQuery(id+"F7.wireOp",EDGE,"E70"),sQuery(id+"F7.wireOp",EDGE,"E70"),sQuery(id+"F7.wireOp",EDGE,"E71"),sQuery(id+"F7.wireOp",EDGE,"E72"),sQuery(id+"F7.wireOp",EDGE,"E73"),sQuery(id+"F7.wireOp",EDGE,"E74"),sQuery(id+"F7.wireOp",EDGE,"E75"),sQuery(id+"F7.wireOp",EDGE,"E76"),sQuery(id+"F7.wireOp",EDGE,"E76"),sQuery(id+"F7.wireOp",EDGE,"E77"),sQuery(id+"F7.wireOp",EDGE,"E78"),sQuery(id+"F7.wireOp",EDGE,"E79"),sQuery(id+"F7.wireOp",EDGE,"E80"),sQuery(id+"F7.wireOp",EDGE,"E81"),sQuery(id+"F7.wireOp",EDGE,"E82"),sQuery(id+"F7.wireOp",EDGE,"E83"),sQuery(id+"F7.wireOp",EDGE,"E84"),sQuery(id+"F7.wireOp",EDGE,"E84"),sQuery(id+"F7.wireOp",EDGE,"E85"),sQuery(id+"F7.wireOp",EDGE,"E86"),sQuery(id+"F7.wireOp",EDGE,"E87"),sQuery(id+"F7.wireOp",EDGE,"E88"),sQuery(id+"F7.wireOp",EDGE,"E89"),sQuery(id+"F7.wireOp",EDGE,"E90"),sQuery(id+"F7.wireOp",EDGE,"E91"),sQuery(id+"F7.wireOp",EDGE,"E92"),sQuery(id+"F7.wireOp",EDGE,"E93"),sQuery(id+"F7.wireOp",EDGE,"E94"),sQuery(id+"F7.wireOp",EDGE,"E95"),sQuery(id+"F7.wireOp",EDGE,"E96"),sQuery(id+"F7.wireOp",EDGE,"E97"),sQuery(id+"F7.wireOp",EDGE,"E98"),sQuery(id+"F7.wireOp",EDGE,"E99"),sQuery(id+"F7.wireOp",EDGE,"E15")])]});
            var Q1;
            Q1=makeQuery(id+"F8.opExtrude","SWEPT_BODY",BODY,{"disambiguationData":[OSD([sQuery(id+"F7.wireOp",EDGE,"E100"),sQuery(id+"F7.wireOp",EDGE,"E101"),sQuery(id+"F7.wireOp",EDGE,"E102"),sQuery(id+"F7.wireOp",EDGE,"E103"),sQuery(id+"F7.wireOp",EDGE,"E103"),sQuery(id+"F7.wireOp",EDGE,"E104"),sQuery(id+"F7.wireOp",EDGE,"E105"),sQuery(id+"F7.wireOp",EDGE,"E106"),sQuery(id+"F7.wireOp",EDGE,"E107"),sQuery(id+"F7.wireOp",EDGE,"E108"),sQuery(id+"F7.wireOp",EDGE,"E109"),sQuery(id+"F7.wireOp",EDGE,"E110"),sQuery(id+"F7.wireOp",EDGE,"E111"),sQuery(id+"F7.wireOp",EDGE,"E112"),sQuery(id+"F7.wireOp",EDGE,"E113"),sQuery(id+"F7.wireOp",EDGE,"E114"),sQuery(id+"F7.wireOp",EDGE,"E115"),sQuery(id+"F7.wireOp",EDGE,"E116"),sQuery(id+"F7.wireOp",EDGE,"E117"),sQuery(id+"F7.wireOp",EDGE,"E118"),sQuery(id+"F7.wireOp",EDGE,"E119"),sQuery(id+"F7.wireOp",EDGE,"E120"),sQuery(id+"F7.wireOp",EDGE,"E121"),sQuery(id+"F7.wireOp",EDGE,"E122"),sQuery(id+"F7.wireOp",EDGE,"E123"),sQuery(id+"F7.wireOp",EDGE,"E124"),sQuery(id+"F7.wireOp",EDGE,"E125"),sQuery(id+"F7.wireOp",EDGE,"E126"),sQuery(id+"F7.wireOp",EDGE,"E127"),sQuery(id+"F7.wireOp",EDGE,"E128"),sQuery(id+"F7.wireOp",EDGE,"E129"),sQuery(id+"F7.wireOp",EDGE,"E130"),sQuery(id+"F7.wireOp",EDGE,"E131"),sQuery(id+"F7.wireOp",EDGE,"E132"),sQuery(id+"F7.wireOp",EDGE,"E133"),sQuery(id+"F7.wireOp",EDGE,"E134"),sQuery(id+"F7.wireOp",EDGE,"E135"),sQuery(id+"F7.wireOp",EDGE,"E136"),sQuery(id+"F7.wireOp",EDGE,"E137"),sQuery(id+"F7.wireOp",EDGE,"E137"),sQuery(id+"F7.wireOp",EDGE,"E138"),sQuery(id+"F7.wireOp",EDGE,"E139"),sQuery(id+"F7.wireOp",EDGE,"E140"),sQuery(id+"F7.wireOp",EDGE,"E141"),sQuery(id+"F7.wireOp",EDGE,"E142"),sQuery(id+"F7.wireOp",EDGE,"E143"),sQuery(id+"F7.wireOp",EDGE,"E144"),sQuery(id+"F7.wireOp",EDGE,"E145"),sQuery(id+"F7.wireOp",EDGE,"E146"),sQuery(id+"F7.wireOp",EDGE,"E147"),sQuery(id+"F7.wireOp",EDGE,"E148"),sQuery(id+"F7.wireOp",EDGE,"E149"),sQuery(id+"F7.wireOp",EDGE,"E150"),sQuery(id+"F7.wireOp",EDGE,"E151"),sQuery(id+"F7.wireOp",EDGE,"E152"),sQuery(id+"F7.wireOp",EDGE,"E153"),sQuery(id+"F7.wireOp",EDGE,"E154"),sQuery(id+"F7.wireOp",EDGE,"E155"),sQuery(id+"F7.wireOp",EDGE,"E156"),sQuery(id+"F7.wireOp",EDGE,"E156"),sQuery(id+"F7.wireOp",EDGE,"E157"),sQuery(id+"F7.wireOp",EDGE,"E158"),sQuery(id+"F7.wireOp",EDGE,"E159"),sQuery(id+"F7.wireOp",EDGE,"E160"),sQuery(id+"F7.wireOp",EDGE,"E161"),sQuery(id+"F7.wireOp",EDGE,"E162"),sQuery(id+"F7.wireOp",EDGE,"E163"),sQuery(id+"F7.wireOp",EDGE,"E164"),sQuery(id+"F7.wireOp",EDGE,"E165"),sQuery(id+"F7.wireOp",EDGE,"E166"),sQuery(id+"F7.wireOp",EDGE,"E167"),sQuery(id+"F7.wireOp",EDGE,"E168"),sQuery(id+"F7.wireOp",EDGE,"E169"),sQuery(id+"F7.wireOp",EDGE,"E170"),sQuery(id+"F7.wireOp",EDGE,"E171")])]});
            var Q2;
            Q2=makeQuery(id+"F8.opExtrude","SWEPT_BODY",BODY,{"disambiguationData":[OSD([sQuery(id+"F7.wireOp",EDGE,"E172"),sQuery(id+"F7.wireOp",EDGE,"E173"),sQuery(id+"F7.wireOp",EDGE,"E174"),sQuery(id+"F7.wireOp",EDGE,"E175"),sQuery(id+"F7.wireOp",EDGE,"E176"),sQuery(id+"F7.wireOp",EDGE,"E177"),sQuery(id+"F7.wireOp",EDGE,"E178"),sQuery(id+"F7.wireOp",EDGE,"E179"),sQuery(id+"F7.wireOp",EDGE,"E180"),sQuery(id+"F7.wireOp",EDGE,"E181"),sQuery(id+"F7.wireOp",EDGE,"E182"),sQuery(id+"F7.wireOp",EDGE,"E183"),sQuery(id+"F7.wireOp",EDGE,"E184"),sQuery(id+"F7.wireOp",EDGE,"E185"),sQuery(id+"F7.wireOp",EDGE,"E186"),sQuery(id+"F7.wireOp",EDGE,"E187"),sQuery(id+"F7.wireOp",EDGE,"E188"),sQuery(id+"F7.wireOp",EDGE,"E189"),sQuery(id+"F7.wireOp",EDGE,"E190"),sQuery(id+"F7.wireOp",EDGE,"E191"),sQuery(id+"F7.wireOp",EDGE,"E192"),sQuery(id+"F7.wireOp",EDGE,"E193"),sQuery(id+"F7.wireOp",EDGE,"E194"),sQuery(id+"F7.wireOp",EDGE,"E195"),sQuery(id+"F7.wireOp",EDGE,"E196"),sQuery(id+"F7.wireOp",EDGE,"E197"),sQuery(id+"F7.wireOp",EDGE,"E198"),sQuery(id+"F7.wireOp",EDGE,"E199"),sQuery(id+"F7.wireOp",EDGE,"E200"),sQuery(id+"F7.wireOp",EDGE,"E200"),sQuery(id+"F7.wireOp",EDGE,"E201"),sQuery(id+"F7.wireOp",EDGE,"E202"),sQuery(id+"F7.wireOp",EDGE,"E203"),sQuery(id+"F7.wireOp",EDGE,"E204"),sQuery(id+"F7.wireOp",EDGE,"E205"),sQuery(id+"F7.wireOp",EDGE,"E206"),sQuery(id+"F7.wireOp",EDGE,"E207"),sQuery(id+"F7.wireOp",EDGE,"E208"),sQuery(id+"F7.wireOp",EDGE,"E209"),sQuery(id+"F7.wireOp",EDGE,"E210"),sQuery(id+"F7.wireOp",EDGE,"E211"),sQuery(id+"F7.wireOp",EDGE,"E212"),sQuery(id+"F7.wireOp",EDGE,"E213"),sQuery(id+"F7.wireOp",EDGE,"E214"),sQuery(id+"F7.wireOp",EDGE,"E215"),sQuery(id+"F7.wireOp",EDGE,"E216"),sQuery(id+"F7.wireOp",EDGE,"E217"),sQuery(id+"F7.wireOp",EDGE,"E218"),sQuery(id+"F7.wireOp",EDGE,"E219"),sQuery(id+"F7.wireOp",EDGE,"E220"),sQuery(id+"F7.wireOp",EDGE,"E221"),sQuery(id+"F7.wireOp",EDGE,"E222"),sQuery(id+"F7.wireOp",EDGE,"E223"),sQuery(id+"F7.wireOp",EDGE,"E224"),sQuery(id+"F7.wireOp",EDGE,"E225"),sQuery(id+"F7.wireOp",EDGE,"E226"),sQuery(id+"F7.wireOp",EDGE,"E227"),sQuery(id+"F7.wireOp",EDGE,"E228"),sQuery(id+"F7.wireOp",EDGE,"E229"),sQuery(id+"F7.wireOp",EDGE,"E230"),sQuery(id+"F7.wireOp",EDGE,"E231"),sQuery(id+"F7.wireOp",EDGE,"E232"),sQuery(id+"F7.wireOp",EDGE,"E233"),sQuery(id+"F7.wireOp",EDGE,"E234"),sQuery(id+"F7.wireOp",EDGE,"E235"),sQuery(id+"F7.wireOp",EDGE,"E236"),sQuery(id+"F7.wireOp",EDGE,"E237"),sQuery(id+"F7.wireOp",EDGE,"E238"),sQuery(id+"F7.wireOp",EDGE,"E239"),sQuery(id+"F7.wireOp",EDGE,"E240"),sQuery(id+"F7.wireOp",EDGE,"E241"),sQuery(id+"F7.wireOp",EDGE,"E242"),sQuery(id+"F7.wireOp",EDGE,"E243"),sQuery(id+"F7.wireOp",EDGE,"E244"),sQuery(id+"F7.wireOp",EDGE,"E245"),sQuery(id+"F7.wireOp",EDGE,"E246"),sQuery(id+"F7.wireOp",EDGE,"E247"),sQuery(id+"F7.wireOp",EDGE,"E248"),sQuery(id+"F7.wireOp",EDGE,"E249"),sQuery(id+"F7.wireOp",EDGE,"E249"),sQuery(id+"F7.wireOp",EDGE,"E250"),sQuery(id+"F7.wireOp",EDGE,"E251"),sQuery(id+"F7.wireOp",EDGE,"E251"),sQuery(id+"F7.wireOp",EDGE,"E252"),sQuery(id+"F7.wireOp",EDGE,"E253"),sQuery(id+"F7.wireOp",EDGE,"E254"),sQuery(id+"F7.wireOp",EDGE,"E255"),sQuery(id+"F7.wireOp",EDGE,"E256"),sQuery(id+"F7.wireOp",EDGE,"E257"),sQuery(id+"F7.wireOp",EDGE,"E258"),sQuery(id+"F7.wireOp",EDGE,"E259"),sQuery(id+"F7.wireOp",EDGE,"E260"),sQuery(id+"F7.wireOp",EDGE,"E261"),sQuery(id+"F7.wireOp",EDGE,"E262"),sQuery(id+"F7.wireOp",EDGE,"E263"),sQuery(id+"F7.wireOp",EDGE,"E264"),sQuery(id+"F7.wireOp",EDGE,"E265"),sQuery(id+"F7.wireOp",EDGE,"E266"),sQuery(id+"F7.wireOp",EDGE,"E267"),sQuery(id+"F7.wireOp",EDGE,"E268"),sQuery(id+"F7.wireOp",EDGE,"E269"),sQuery(id+"F7.wireOp",EDGE,"E270"),sQuery(id+"F7.wireOp",EDGE,"E271"),sQuery(id+"F7.wireOp",EDGE,"E272"),sQuery(id+"F7.wireOp",EDGE,"E273"),sQuery(id+"F7.wireOp",EDGE,"E274"),sQuery(id+"F7.wireOp",EDGE,"E275"),sQuery(id+"F7.wireOp",EDGE,"E276"),sQuery(id+"F7.wireOp",EDGE,"E277"),sQuery(id+"F7.wireOp",EDGE,"E278"),sQuery(id+"F7.wireOp",EDGE,"E279"),sQuery(id+"F7.wireOp",EDGE,"E280"),sQuery(id+"F7.wireOp",EDGE,"E281"),sQuery(id+"F7.wireOp",EDGE,"E282"),sQuery(id+"F7.wireOp",EDGE,"E283"),sQuery(id+"F7.wireOp",EDGE,"E284"),sQuery(id+"F7.wireOp",EDGE,"E285"),sQuery(id+"F7.wireOp",EDGE,"E286"),sQuery(id+"F7.wireOp",EDGE,"E287"),sQuery(id+"F7.wireOp",EDGE,"E288"),sQuery(id+"F7.wireOp",EDGE,"E289"),sQuery(id+"F7.wireOp",EDGE,"E290"),sQuery(id+"F7.wireOp",EDGE,"E291"),sQuery(id+"F7.wireOp",EDGE,"E292"),sQuery(id+"F7.wireOp",EDGE,"E293"),sQuery(id+"F7.wireOp",EDGE,"E294"),sQuery(id+"F7.wireOp",EDGE,"E295"),sQuery(id+"F7.wireOp",EDGE,"E296"),sQuery(id+"F7.wireOp",EDGE,"E296"),sQuery(id+"F7.wireOp",EDGE,"E297"),sQuery(id+"F7.wireOp",EDGE,"E298"),sQuery(id+"F7.wireOp",EDGE,"E299"),sQuery(id+"F7.wireOp",EDGE,"E300"),sQuery(id+"F7.wireOp",EDGE,"E301"),sQuery(id+"F7.wireOp",EDGE,"E302"),sQuery(id+"F7.wireOp",EDGE,"E303")])]});
            var Q3;
            Q3=makeQuery(id+"F8.opExtrude","SWEPT_BODY",BODY,{"disambiguationData":[OSD([sQuery(id+"F7.wireOp",EDGE,"E304"),sQuery(id+"F7.wireOp",EDGE,"E305"),sQuery(id+"F7.wireOp",EDGE,"E306"),sQuery(id+"F7.wireOp",EDGE,"E307"),sQuery(id+"F7.wireOp",EDGE,"E308"),sQuery(id+"F7.wireOp",EDGE,"E309"),sQuery(id+"F7.wireOp",EDGE,"E310"),sQuery(id+"F7.wireOp",EDGE,"E311"),sQuery(id+"F7.wireOp",EDGE,"E312"),sQuery(id+"F7.wireOp",EDGE,"E313"),sQuery(id+"F7.wireOp",EDGE,"E314"),sQuery(id+"F7.wireOp",EDGE,"E315"),sQuery(id+"F7.wireOp",EDGE,"E316"),sQuery(id+"F7.wireOp",EDGE,"E317"),sQuery(id+"F7.wireOp",EDGE,"E318"),sQuery(id+"F7.wireOp",EDGE,"E319"),sQuery(id+"F7.wireOp",EDGE,"E320"),sQuery(id+"F7.wireOp",EDGE,"E321"),sQuery(id+"F7.wireOp",EDGE,"E322"),sQuery(id+"F7.wireOp",EDGE,"E323"),sQuery(id+"F7.wireOp",EDGE,"E324"),sQuery(id+"F7.wireOp",EDGE,"E325"),sQuery(id+"F7.wireOp",EDGE,"E326"),sQuery(id+"F7.wireOp",EDGE,"E327"),sQuery(id+"F7.wireOp",EDGE,"E327"),sQuery(id+"F7.wireOp",EDGE,"E328"),sQuery(id+"F7.wireOp",EDGE,"E329"),sQuery(id+"F7.wireOp",EDGE,"E330"),sQuery(id+"F7.wireOp",EDGE,"E331"),sQuery(id+"F7.wireOp",EDGE,"E332"),sQuery(id+"F7.wireOp",EDGE,"E332"),sQuery(id+"F7.wireOp",EDGE,"E333"),sQuery(id+"F7.wireOp",EDGE,"E334"),sQuery(id+"F7.wireOp",EDGE,"E335"),sQuery(id+"F7.wireOp",EDGE,"E336"),sQuery(id+"F7.wireOp",EDGE,"E337"),sQuery(id+"F7.wireOp",EDGE,"E337"),sQuery(id+"F7.wireOp",EDGE,"E338"),sQuery(id+"F7.wireOp",EDGE,"E339"),sQuery(id+"F7.wireOp",EDGE,"E340"),sQuery(id+"F7.wireOp",EDGE,"E341"),sQuery(id+"F7.wireOp",EDGE,"E342"),sQuery(id+"F7.wireOp",EDGE,"E342"),sQuery(id+"F7.wireOp",EDGE,"E343"),sQuery(id+"F7.wireOp",EDGE,"E344"),sQuery(id+"F7.wireOp",EDGE,"E345"),sQuery(id+"F7.wireOp",EDGE,"E346"),sQuery(id+"F7.wireOp",EDGE,"E347"),sQuery(id+"F7.wireOp",EDGE,"E348"),sQuery(id+"F7.wireOp",EDGE,"E349"),sQuery(id+"F7.wireOp",EDGE,"E350"),sQuery(id+"F7.wireOp",EDGE,"E351"),sQuery(id+"F7.wireOp",EDGE,"E352"),sQuery(id+"F7.wireOp",EDGE,"E353"),sQuery(id+"F7.wireOp",EDGE,"E354"),sQuery(id+"F7.wireOp",EDGE,"E355"),sQuery(id+"F7.wireOp",EDGE,"E356"),sQuery(id+"F7.wireOp",EDGE,"E357"),sQuery(id+"F7.wireOp",EDGE,"E358"),sQuery(id+"F7.wireOp",EDGE,"E358"),sQuery(id+"F7.wireOp",EDGE,"E359"),sQuery(id+"F7.wireOp",EDGE,"E360"),sQuery(id+"F7.wireOp",EDGE,"E361"),sQuery(id+"F7.wireOp",EDGE,"E362"),sQuery(id+"F7.wireOp",EDGE,"E363")])]});
            var Q4;
            Q4=makeQuery(id+"F8.opExtrude","SWEPT_BODY",BODY,{"disambiguationData":[OSD([sQuery(id+"F7.wireOp",EDGE,"E364"),sQuery(id+"F7.wireOp",EDGE,"E365"),sQuery(id+"F7.wireOp",EDGE,"E366"),sQuery(id+"F7.wireOp",EDGE,"E367"),sQuery(id+"F7.wireOp",EDGE,"E368"),sQuery(id+"F7.wireOp",EDGE,"E369"),sQuery(id+"F7.wireOp",EDGE,"E370"),sQuery(id+"F7.wireOp",EDGE,"E371"),sQuery(id+"F7.wireOp",EDGE,"E372"),sQuery(id+"F7.wireOp",EDGE,"E373"),sQuery(id+"F7.wireOp",EDGE,"E374"),sQuery(id+"F7.wireOp",EDGE,"E375"),sQuery(id+"F7.wireOp",EDGE,"E376"),sQuery(id+"F7.wireOp",EDGE,"E377"),sQuery(id+"F7.wireOp",EDGE,"E378"),sQuery(id+"F7.wireOp",EDGE,"E379"),sQuery(id+"F7.wireOp",EDGE,"E380"),sQuery(id+"F7.wireOp",EDGE,"E381"),sQuery(id+"F7.wireOp",EDGE,"E382"),sQuery(id+"F7.wireOp",EDGE,"E383"),sQuery(id+"F7.wireOp",EDGE,"E384"),sQuery(id+"F7.wireOp",EDGE,"E385"),sQuery(id+"F7.wireOp",EDGE,"E386"),sQuery(id+"F7.wireOp",EDGE,"E387"),sQuery(id+"F7.wireOp",EDGE,"E388"),sQuery(id+"F7.wireOp",EDGE,"E389"),sQuery(id+"F7.wireOp",EDGE,"E390"),sQuery(id+"F7.wireOp",EDGE,"E391"),sQuery(id+"F7.wireOp",EDGE,"E392"),sQuery(id+"F7.wireOp",EDGE,"E393"),sQuery(id+"F7.wireOp",EDGE,"E394"),sQuery(id+"F7.wireOp",EDGE,"E395"),sQuery(id+"F7.wireOp",EDGE,"E396"),sQuery(id+"F7.wireOp",EDGE,"E397"),sQuery(id+"F7.wireOp",EDGE,"E398"),sQuery(id+"F7.wireOp",EDGE,"E399"),sQuery(id+"F7.wireOp",EDGE,"E400"),sQuery(id+"F7.wireOp",EDGE,"E401"),sQuery(id+"F7.wireOp",EDGE,"E402"),sQuery(id+"F7.wireOp",EDGE,"E403"),sQuery(id+"F7.wireOp",EDGE,"E404"),sQuery(id+"F7.wireOp",EDGE,"E405"),sQuery(id+"F7.wireOp",EDGE,"E406"),sQuery(id+"F7.wireOp",EDGE,"E407"),sQuery(id+"F7.wireOp",EDGE,"E408"),sQuery(id+"F7.wireOp",EDGE,"E409"),sQuery(id+"F7.wireOp",EDGE,"E410"),sQuery(id+"F7.wireOp",EDGE,"E411"),sQuery(id+"F7.wireOp",EDGE,"E412"),sQuery(id+"F7.wireOp",EDGE,"E413"),sQuery(id+"F7.wireOp",EDGE,"E414"),sQuery(id+"F7.wireOp",EDGE,"E415"),sQuery(id+"F7.wireOp",EDGE,"E416"),sQuery(id+"F7.wireOp",EDGE,"E417"),sQuery(id+"F7.wireOp",EDGE,"E418"),sQuery(id+"F7.wireOp",EDGE,"E419"),sQuery(id+"F7.wireOp",EDGE,"E420"),sQuery(id+"F7.wireOp",EDGE,"E421"),sQuery(id+"F7.wireOp",EDGE,"E422"),sQuery(id+"F7.wireOp",EDGE,"E423"),sQuery(id+"F7.wireOp",EDGE,"E424"),sQuery(id+"F7.wireOp",EDGE,"E425"),sQuery(id+"F7.wireOp",EDGE,"E426"),sQuery(id+"F7.wireOp",EDGE,"E427"),sQuery(id+"F7.wireOp",EDGE,"E428"),sQuery(id+"F7.wireOp",EDGE,"E429"),sQuery(id+"F7.wireOp",EDGE,"E430"),sQuery(id+"F7.wireOp",EDGE,"E431"),sQuery(id+"F7.wireOp",EDGE,"E432"),sQuery(id+"F7.wireOp",EDGE,"E433"),sQuery(id+"F7.wireOp",EDGE,"E434"),sQuery(id+"F7.wireOp",EDGE,"E435"),sQuery(id+"F7.wireOp",EDGE,"E436"),sQuery(id+"F7.wireOp",EDGE,"E437"),sQuery(id+"F7.wireOp",EDGE,"E438"),sQuery(id+"F7.wireOp",EDGE,"E439"),sQuery(id+"F7.wireOp",EDGE,"E440"),sQuery(id+"F7.wireOp",EDGE,"E441"),sQuery(id+"F7.wireOp",EDGE,"E442"),sQuery(id+"F7.wireOp",EDGE,"E443"),sQuery(id+"F7.wireOp",EDGE,"E444")])]});
            var Q5;
            Q5=makeQuery(id+"F8.opExtrude","CAP_VERTEX",VERTEX,{"disambiguationData":[OSD([sQuery(id+"F7.wireOp",EDGE,"E67"),sQuery(id+"F7.wireOp",EDGE,"E68")])],"isStart":false});
            transform(context, id + "F10", {"entities" : qUnion([Q0, Q1, Q2, Q3, Q4]), "transformType" : TransformType.TRANSLATION_3D, "dx" : 24 * mm, "dy" : 0 * mm, "dz" : -20 * mm, "makeCopy" : false});
        }
    });
